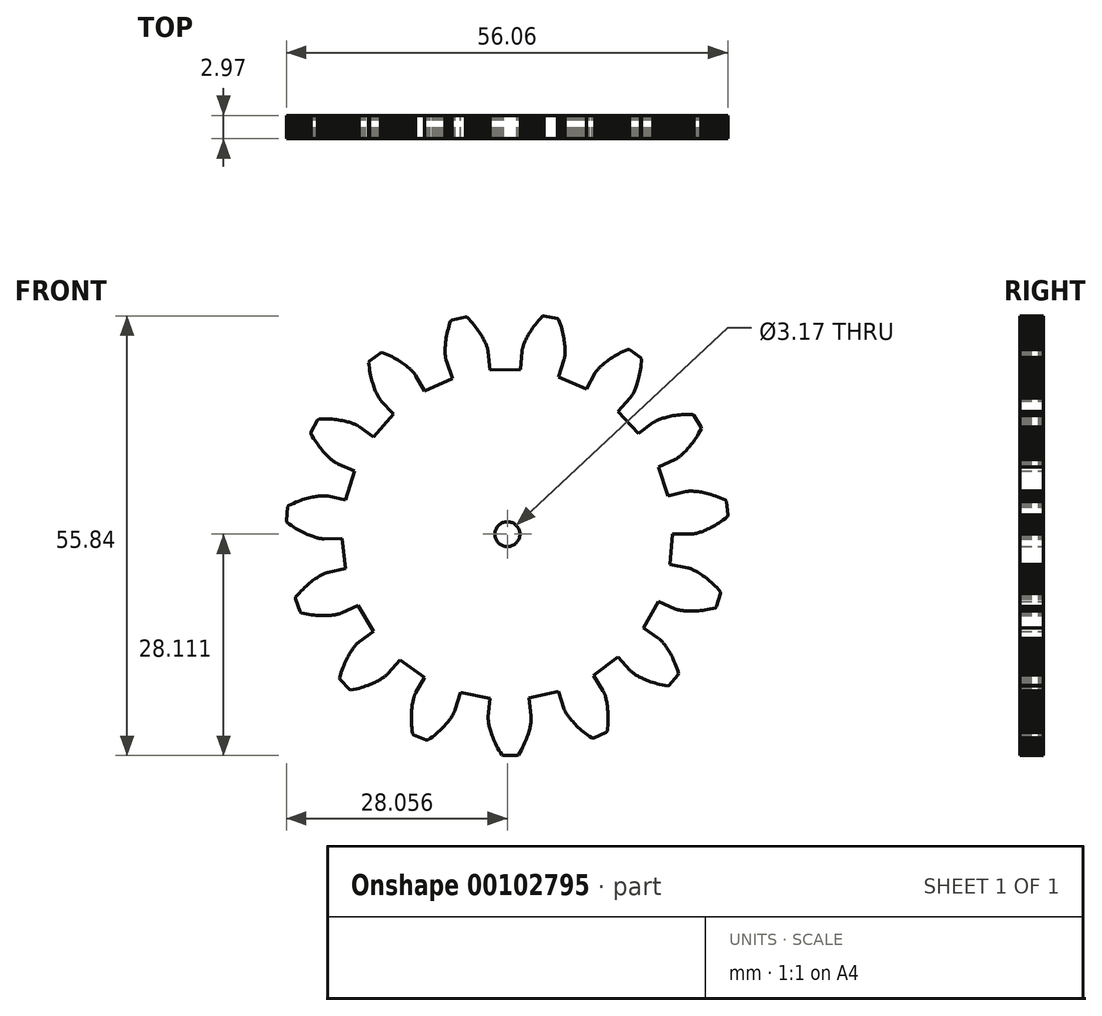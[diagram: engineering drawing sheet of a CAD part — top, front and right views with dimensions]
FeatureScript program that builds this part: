
annotation { "Feature Type Name" : "Feature", "Feature Type Description" : "" }
export const myFeature = defineFeature(function(context is Context, id is Id, definition is map)
    precondition{}
    {
        {
            var Q0;
            Q0=qCreatedBy(makeId("Front.planeOp"),FACE);
            var sketch = newSketch(context, id + "F0", { "sketchPlane" : qUnion([Q0])});
            skLineSegment(sketch, "E0", {"start": v(21.03, 0.2) * mm, "end": v(23.35, 0.2) * mm});
            skLineSegment(sketch, "E1", {"start": v(23.35, 0.2) * mm, "end": v(23.38, 0.2) * mm});
            skLineSegment(sketch, "E2", {"start": v(23.38, 0.2) * mm, "end": v(23.42, 0.2) * mm});
            skLineSegment(sketch, "E3", {"start": v(23.42, 0.2) * mm, "end": v(23.48, 0.2) * mm});
            skLineSegment(sketch, "E4", {"start": v(23.48, 0.2) * mm, "end": v(23.54, 0.2) * mm});
            skLineSegment(sketch, "E5", {"start": v(23.54, 0.2) * mm, "end": v(23.62, 0.22) * mm});
            skLineSegment(sketch, "E6", {"start": v(23.62, 0.22) * mm, "end": v(23.71, 0.24) * mm});
            skLineSegment(sketch, "E7", {"start": v(23.71, 0.24) * mm, "end": v(23.81, 0.26) * mm});
            skLineSegment(sketch, "E8", {"start": v(23.81, 0.26) * mm, "end": v(23.93, 0.28) * mm});
            skLineSegment(sketch, "E9", {"start": v(23.93, 0.28) * mm, "end": v(24.05, 0.31) * mm});
            skLineSegment(sketch, "E10", {"start": v(24.05, 0.31) * mm, "end": v(24.2, 0.35) * mm});
            skLineSegment(sketch, "E11", {"start": v(24.2, 0.35) * mm, "end": v(24.34, 0.4) * mm});
            skLineSegment(sketch, "E12", {"start": v(24.34, 0.4) * mm, "end": v(24.5, 0.44) * mm});
            skLineSegment(sketch, "E13", {"start": v(24.5, 0.44) * mm, "end": v(24.67, 0.5) * mm});
            skLineSegment(sketch, "E14", {"start": v(24.67, 0.5) * mm, "end": v(24.85, 0.57) * mm});
            skLineSegment(sketch, "E15", {"start": v(24.85, 0.57) * mm, "end": v(25.04, 0.64) * mm});
            skLineSegment(sketch, "E16", {"start": v(25.04, 0.64) * mm, "end": v(25.24, 0.73) * mm});
            skLineSegment(sketch, "E17", {"start": v(25.24, 0.73) * mm, "end": v(25.45, 0.83) * mm});
            skLineSegment(sketch, "E18", {"start": v(25.45, 0.83) * mm, "end": v(25.67, 0.93) * mm});
            skLineSegment(sketch, "E19", {"start": v(25.67, 0.93) * mm, "end": v(25.9, 1.05) * mm});
            skLineSegment(sketch, "E20", {"start": v(25.9, 1.05) * mm, "end": v(26.13, 1.17) * mm});
            skLineSegment(sketch, "E21", {"start": v(26.13, 1.17) * mm, "end": v(26.38, 1.31) * mm});
            skLineSegment(sketch, "E22", {"start": v(26.38, 1.31) * mm, "end": v(26.63, 1.46) * mm});
            skLineSegment(sketch, "E23", {"start": v(26.63, 1.46) * mm, "end": v(26.89, 1.63) * mm});
            skLineSegment(sketch, "E24", {"start": v(26.89, 1.63) * mm, "end": v(27.15, 1.8) * mm});
            skLineSegment(sketch, "E25", {"start": v(27.15, 1.8) * mm, "end": v(27.42, 2) * mm});
            skLineSegment(sketch, "E26", {"start": v(27.42, 2) * mm, "end": v(27.7, 2.2) * mm});
            skLineSegment(sketch, "E27", {"start": v(27.7, 2.2) * mm, "end": v(27.98, 2.42) * mm});
            skLineSegment(sketch, "E28", {"start": v(27.98, 2.42) * mm, "end": v(28.03, 2.63) * mm});
            skLineSegment(sketch, "E29", {"start": v(28.03, 2.63) * mm, "end": v(27.83, 4.33) * mm});
            skLineSegment(sketch, "E30", {"start": v(27.83, 4.33) * mm, "end": v(27.73, 4.53) * mm});
            skLineSegment(sketch, "E31", {"start": v(27.73, 4.53) * mm, "end": v(27.4, 4.67) * mm});
            skLineSegment(sketch, "E32", {"start": v(27.4, 4.67) * mm, "end": v(27.1, 4.8) * mm});
            skLineSegment(sketch, "E33", {"start": v(27.1, 4.8) * mm, "end": v(26.78, 4.93) * mm});
            skLineSegment(sketch, "E34", {"start": v(26.78, 4.93) * mm, "end": v(26.48, 5.04) * mm});
            skLineSegment(sketch, "E35", {"start": v(26.48, 5.04) * mm, "end": v(26.2, 5.14) * mm});
            skLineSegment(sketch, "E36", {"start": v(26.2, 5.14) * mm, "end": v(25.91, 5.23) * mm});
            skLineSegment(sketch, "E37", {"start": v(25.91, 5.23) * mm, "end": v(25.65, 5.3) * mm});
            skLineSegment(sketch, "E38", {"start": v(25.65, 5.3) * mm, "end": v(25.39, 5.37) * mm});
            skLineSegment(sketch, "E39", {"start": v(25.39, 5.37) * mm, "end": v(25.14, 5.44) * mm});
            skLineSegment(sketch, "E40", {"start": v(25.14, 5.44) * mm, "end": v(24.9, 5.49) * mm});
            skLineSegment(sketch, "E41", {"start": v(24.9, 5.49) * mm, "end": v(24.67, 5.53) * mm});
            skLineSegment(sketch, "E42", {"start": v(24.67, 5.53) * mm, "end": v(24.46, 5.57) * mm});
            skLineSegment(sketch, "E43", {"start": v(24.46, 5.57) * mm, "end": v(24.26, 5.6) * mm});
            skLineSegment(sketch, "E44", {"start": v(24.26, 5.6) * mm, "end": v(24.06, 5.62) * mm});
            skLineSegment(sketch, "E45", {"start": v(24.06, 5.62) * mm, "end": v(23.89, 5.64) * mm});
            skLineSegment(sketch, "E46", {"start": v(23.89, 5.64) * mm, "end": v(23.72, 5.65) * mm});
            skLineSegment(sketch, "E47", {"start": v(23.72, 5.65) * mm, "end": v(23.56, 5.66) * mm});
            skLineSegment(sketch, "E48", {"start": v(23.56, 5.66) * mm, "end": v(23.42, 5.66) * mm});
            skLineSegment(sketch, "E49", {"start": v(23.42, 5.66) * mm, "end": v(23.3, 5.66) * mm});
            skLineSegment(sketch, "E50", {"start": v(23.3, 5.66) * mm, "end": v(23.18, 5.66) * mm});
            skLineSegment(sketch, "E51", {"start": v(23.18, 5.66) * mm, "end": v(23.07, 5.65) * mm});
            skLineSegment(sketch, "E52", {"start": v(23.07, 5.65) * mm, "end": v(22.98, 5.65) * mm});
            skLineSegment(sketch, "E53", {"start": v(22.98, 5.65) * mm, "end": v(22.9, 5.64) * mm});
            skLineSegment(sketch, "E54", {"start": v(22.9, 5.64) * mm, "end": v(22.84, 5.63) * mm});
            skLineSegment(sketch, "E55", {"start": v(22.84, 5.63) * mm, "end": v(22.78, 5.63) * mm});
            skLineSegment(sketch, "E56", {"start": v(22.78, 5.63) * mm, "end": v(22.74, 5.62) * mm});
            skLineSegment(sketch, "E57", {"start": v(22.74, 5.62) * mm, "end": v(22.72, 5.61) * mm});
            skLineSegment(sketch, "E58", {"start": v(22.72, 5.61) * mm, "end": v(22.7, 5.61) * mm});
            skLineSegment(sketch, "E59", {"start": v(22.7, 5.61) * mm, "end": v(20.45, 5.07) * mm});
            skLineSegment(sketch, "E60", {"start": v(20.45, 5.07) * mm, "end": v(19.21, 8.73) * mm});
            skLineSegment(sketch, "E61", {"start": v(19.21, 8.73) * mm, "end": v(21.32, 9.67) * mm});
            skLineSegment(sketch, "E62", {"start": v(21.32, 9.67) * mm, "end": v(21.34, 9.68) * mm});
            skLineSegment(sketch, "E63", {"start": v(21.34, 9.68) * mm, "end": v(21.36, 9.7) * mm});
            skLineSegment(sketch, "E64", {"start": v(21.36, 9.7) * mm, "end": v(21.4, 9.71) * mm});
            skLineSegment(sketch, "E65", {"start": v(21.4, 9.71) * mm, "end": v(21.45, 9.74) * mm});
            skLineSegment(sketch, "E66", {"start": v(21.45, 9.74) * mm, "end": v(21.5, 9.77) * mm});
            skLineSegment(sketch, "E67", {"start": v(21.5, 9.77) * mm, "end": v(21.57, 9.82) * mm});
            skLineSegment(sketch, "E68", {"start": v(21.57, 9.82) * mm, "end": v(21.64, 9.87) * mm});
            skLineSegment(sketch, "E69", {"start": v(21.64, 9.87) * mm, "end": v(21.73, 9.93) * mm});
            skLineSegment(sketch, "E70", {"start": v(21.73, 9.93) * mm, "end": v(21.82, 10) * mm});
            skLineSegment(sketch, "E71", {"start": v(21.82, 10) * mm, "end": v(21.93, 10.07) * mm});
            skLineSegment(sketch, "E72", {"start": v(21.93, 10.07) * mm, "end": v(22.04, 10.16) * mm});
            skLineSegment(sketch, "E73", {"start": v(22.04, 10.16) * mm, "end": v(22.15, 10.26) * mm});
            skLineSegment(sketch, "E74", {"start": v(22.15, 10.26) * mm, "end": v(22.28, 10.38) * mm});
            skLineSegment(sketch, "E75", {"start": v(22.28, 10.38) * mm, "end": v(22.41, 10.5) * mm});
            skLineSegment(sketch, "E76", {"start": v(22.41, 10.5) * mm, "end": v(22.55, 10.63) * mm});
            skLineSegment(sketch, "E77", {"start": v(22.55, 10.63) * mm, "end": v(22.7, 10.78) * mm});
            skLineSegment(sketch, "E78", {"start": v(22.7, 10.78) * mm, "end": v(22.84, 10.94) * mm});
            skLineSegment(sketch, "E79", {"start": v(22.84, 10.94) * mm, "end": v(23, 11.11) * mm});
            skLineSegment(sketch, "E80", {"start": v(23, 11.11) * mm, "end": v(23.15, 11.3) * mm});
            skLineSegment(sketch, "E81", {"start": v(23.15, 11.3) * mm, "end": v(23.31, 11.5) * mm});
            skLineSegment(sketch, "E82", {"start": v(23.31, 11.5) * mm, "end": v(23.48, 11.7) * mm});
            skLineSegment(sketch, "E83", {"start": v(23.48, 11.7) * mm, "end": v(23.64, 11.93) * mm});
            skLineSegment(sketch, "E84", {"start": v(23.64, 11.93) * mm, "end": v(23.81, 12.17) * mm});
            skLineSegment(sketch, "E85", {"start": v(23.81, 12.17) * mm, "end": v(23.98, 12.43) * mm});
            skLineSegment(sketch, "E86", {"start": v(23.98, 12.43) * mm, "end": v(24.15, 12.7) * mm});
            skLineSegment(sketch, "E87", {"start": v(24.15, 12.7) * mm, "end": v(24.32, 12.98) * mm});
            skLineSegment(sketch, "E88", {"start": v(24.32, 12.98) * mm, "end": v(24.5, 13.28) * mm});
            skLineSegment(sketch, "E89", {"start": v(24.5, 13.28) * mm, "end": v(24.66, 13.6) * mm});
            skLineSegment(sketch, "E90", {"start": v(24.66, 13.6) * mm, "end": v(24.62, 13.8) * mm});
            skLineSegment(sketch, "E91", {"start": v(24.62, 13.8) * mm, "end": v(23.74, 15.29) * mm});
            skLineSegment(sketch, "E92", {"start": v(23.74, 15.29) * mm, "end": v(23.57, 15.42) * mm});
            skLineSegment(sketch, "E93", {"start": v(23.57, 15.42) * mm, "end": v(23.22, 15.42) * mm});
            skLineSegment(sketch, "E94", {"start": v(23.22, 15.42) * mm, "end": v(22.87, 15.42) * mm});
            skLineSegment(sketch, "E95", {"start": v(22.87, 15.42) * mm, "end": v(22.54, 15.4) * mm});
            skLineSegment(sketch, "E96", {"start": v(22.54, 15.4) * mm, "end": v(22.23, 15.38) * mm});
            skLineSegment(sketch, "E97", {"start": v(22.23, 15.38) * mm, "end": v(21.92, 15.36) * mm});
            skLineSegment(sketch, "E98", {"start": v(21.92, 15.36) * mm, "end": v(21.63, 15.32) * mm});
            skLineSegment(sketch, "E99", {"start": v(21.63, 15.32) * mm, "end": v(21.35, 15.28) * mm});
            skLineSegment(sketch, "E100", {"start": v(21.35, 15.28) * mm, "end": v(21.09, 15.24) * mm});
            skLineSegment(sketch, "E101", {"start": v(21.09, 15.24) * mm, "end": v(20.83, 15.2) * mm});
            skLineSegment(sketch, "E102", {"start": v(20.83, 15.2) * mm, "end": v(20.6, 15.15) * mm});
            skLineSegment(sketch, "E103", {"start": v(20.6, 15.15) * mm, "end": v(20.37, 15.1) * mm});
            skLineSegment(sketch, "E104", {"start": v(20.37, 15.1) * mm, "end": v(20.16, 15.04) * mm});
            skLineSegment(sketch, "E105", {"start": v(20.16, 15.04) * mm, "end": v(19.96, 14.98) * mm});
            skLineSegment(sketch, "E106", {"start": v(19.96, 14.98) * mm, "end": v(19.78, 14.93) * mm});
            skLineSegment(sketch, "E107", {"start": v(19.78, 14.93) * mm, "end": v(19.6, 14.87) * mm});
            skLineSegment(sketch, "E108", {"start": v(19.6, 14.87) * mm, "end": v(19.45, 14.81) * mm});
            skLineSegment(sketch, "E109", {"start": v(19.45, 14.81) * mm, "end": v(19.3, 14.76) * mm});
            skLineSegment(sketch, "E110", {"start": v(19.3, 14.76) * mm, "end": v(19.18, 14.7) * mm});
            skLineSegment(sketch, "E111", {"start": v(19.18, 14.7) * mm, "end": v(19.06, 14.65) * mm});
            skLineSegment(sketch, "E112", {"start": v(19.06, 14.65) * mm, "end": v(18.95, 14.6) * mm});
            skLineSegment(sketch, "E113", {"start": v(18.95, 14.6) * mm, "end": v(18.86, 14.55) * mm});
            skLineSegment(sketch, "E114", {"start": v(18.86, 14.55) * mm, "end": v(18.78, 14.51) * mm});
            skLineSegment(sketch, "E115", {"start": v(18.78, 14.51) * mm, "end": v(18.7, 14.47) * mm});
            skLineSegment(sketch, "E116", {"start": v(18.7, 14.47) * mm, "end": v(18.65, 14.44) * mm});
            skLineSegment(sketch, "E117", {"start": v(18.65, 14.44) * mm, "end": v(18.6, 14.41) * mm});
            skLineSegment(sketch, "E118", {"start": v(18.6, 14.41) * mm, "end": v(18.57, 14.4) * mm});
            skLineSegment(sketch, "E119", {"start": v(18.57, 14.4) * mm, "end": v(18.55, 14.37) * mm});
            skLineSegment(sketch, "E120", {"start": v(18.55, 14.37) * mm, "end": v(18.53, 14.36) * mm});
            skLineSegment(sketch, "E121", {"start": v(18.53, 14.36) * mm, "end": v(16.7, 12.96) * mm});
            skLineSegment(sketch, "E122", {"start": v(16.7, 12.96) * mm, "end": v(14.08, 15.8) * mm});
            skLineSegment(sketch, "E123", {"start": v(14.08, 15.8) * mm, "end": v(15.63, 17.52) * mm});
            skLineSegment(sketch, "E124", {"start": v(15.63, 17.52) * mm, "end": v(15.64, 17.53) * mm});
            skLineSegment(sketch, "E125", {"start": v(15.64, 17.53) * mm, "end": v(15.65, 17.55) * mm});
            skLineSegment(sketch, "E126", {"start": v(15.65, 17.55) * mm, "end": v(15.68, 17.58) * mm});
            skLineSegment(sketch, "E127", {"start": v(15.68, 17.58) * mm, "end": v(15.7, 17.63) * mm});
            skLineSegment(sketch, "E128", {"start": v(15.7, 17.63) * mm, "end": v(15.75, 17.68) * mm});
            skLineSegment(sketch, "E129", {"start": v(15.75, 17.68) * mm, "end": v(15.8, 17.75) * mm});
            skLineSegment(sketch, "E130", {"start": v(15.8, 17.75) * mm, "end": v(15.84, 17.82) * mm});
            skLineSegment(sketch, "E131", {"start": v(15.84, 17.82) * mm, "end": v(15.9, 17.91) * mm});
            skLineSegment(sketch, "E132", {"start": v(15.9, 17.91) * mm, "end": v(15.95, 18.01) * mm});
            skLineSegment(sketch, "E133", {"start": v(15.95, 18.01) * mm, "end": v(16.01, 18.13) * mm});
            skLineSegment(sketch, "E134", {"start": v(16.01, 18.13) * mm, "end": v(16.08, 18.25) * mm});
            skLineSegment(sketch, "E135", {"start": v(16.08, 18.25) * mm, "end": v(16.14, 18.4) * mm});
            skLineSegment(sketch, "E136", {"start": v(16.14, 18.4) * mm, "end": v(16.21, 18.55) * mm});
            skLineSegment(sketch, "E137", {"start": v(16.21, 18.55) * mm, "end": v(16.28, 18.71) * mm});
            skLineSegment(sketch, "E138", {"start": v(16.28, 18.71) * mm, "end": v(16.35, 18.9) * mm});
            skLineSegment(sketch, "E139", {"start": v(16.35, 18.9) * mm, "end": v(16.43, 19.08) * mm});
            skLineSegment(sketch, "E140", {"start": v(16.43, 19.08) * mm, "end": v(16.5, 19.29) * mm});
            skLineSegment(sketch, "E141", {"start": v(16.5, 19.29) * mm, "end": v(16.57, 19.5) * mm});
            skLineSegment(sketch, "E142", {"start": v(16.57, 19.5) * mm, "end": v(16.64, 19.74) * mm});
            skLineSegment(sketch, "E143", {"start": v(16.64, 19.74) * mm, "end": v(16.7, 19.99) * mm});
            skLineSegment(sketch, "E144", {"start": v(16.7, 19.99) * mm, "end": v(16.77, 20.25) * mm});
            skLineSegment(sketch, "E145", {"start": v(16.77, 20.25) * mm, "end": v(16.82, 20.52) * mm});
            skLineSegment(sketch, "E146", {"start": v(16.82, 20.52) * mm, "end": v(16.88, 20.81) * mm});
            skLineSegment(sketch, "E147", {"start": v(16.88, 20.81) * mm, "end": v(16.93, 21.11) * mm});
            skLineSegment(sketch, "E148", {"start": v(16.93, 21.11) * mm, "end": v(16.98, 21.43) * mm});
            skLineSegment(sketch, "E149", {"start": v(16.98, 21.43) * mm, "end": v(17.02, 21.76) * mm});
            skLineSegment(sketch, "E150", {"start": v(17.02, 21.76) * mm, "end": v(17.05, 22.1) * mm});
            skLineSegment(sketch, "E151", {"start": v(17.05, 22.1) * mm, "end": v(17.08, 22.46) * mm});
            skLineSegment(sketch, "E152", {"start": v(17.08, 22.46) * mm, "end": v(16.96, 22.63) * mm});
            skLineSegment(sketch, "E153", {"start": v(16.96, 22.63) * mm, "end": v(15.55, 23.63) * mm});
            skLineSegment(sketch, "E154", {"start": v(15.55, 23.63) * mm, "end": v(15.34, 23.68) * mm});
            skLineSegment(sketch, "E155", {"start": v(15.34, 23.68) * mm, "end": v(15.02, 23.54) * mm});
            skLineSegment(sketch, "E156", {"start": v(15.02, 23.54) * mm, "end": v(14.7, 23.4) * mm});
            skLineSegment(sketch, "E157", {"start": v(14.7, 23.4) * mm, "end": v(14.4, 23.25) * mm});
            skLineSegment(sketch, "E158", {"start": v(14.4, 23.25) * mm, "end": v(14.13, 23.1) * mm});
            skLineSegment(sketch, "E159", {"start": v(14.13, 23.1) * mm, "end": v(13.86, 22.95) * mm});
            skLineSegment(sketch, "E160", {"start": v(13.86, 22.95) * mm, "end": v(13.6, 22.8) * mm});
            skLineSegment(sketch, "E161", {"start": v(13.6, 22.8) * mm, "end": v(13.37, 22.65) * mm});
            skLineSegment(sketch, "E162", {"start": v(13.37, 22.65) * mm, "end": v(13.14, 22.5) * mm});
            skLineSegment(sketch, "E163", {"start": v(13.14, 22.5) * mm, "end": v(12.93, 22.36) * mm});
            skLineSegment(sketch, "E164", {"start": v(12.93, 22.36) * mm, "end": v(12.73, 22.22) * mm});
            skLineSegment(sketch, "E165", {"start": v(12.73, 22.22) * mm, "end": v(12.55, 22.08) * mm});
            skLineSegment(sketch, "E166", {"start": v(12.55, 22.08) * mm, "end": v(12.38, 21.95) * mm});
            skLineSegment(sketch, "E167", {"start": v(12.38, 21.95) * mm, "end": v(12.22, 21.81) * mm});
            skLineSegment(sketch, "E168", {"start": v(12.22, 21.81) * mm, "end": v(12.08, 21.69) * mm});
            skLineSegment(sketch, "E169", {"start": v(12.08, 21.69) * mm, "end": v(11.94, 21.57) * mm});
            skLineSegment(sketch, "E170", {"start": v(11.94, 21.57) * mm, "end": v(11.82, 21.45) * mm});
            skLineSegment(sketch, "E171", {"start": v(11.82, 21.45) * mm, "end": v(11.72, 21.34) * mm});
            skLineSegment(sketch, "E172", {"start": v(11.72, 21.34) * mm, "end": v(11.62, 21.24) * mm});
            skLineSegment(sketch, "E173", {"start": v(11.62, 21.24) * mm, "end": v(11.53, 21.14) * mm});
            skLineSegment(sketch, "E174", {"start": v(11.53, 21.14) * mm, "end": v(11.45, 21.05) * mm});
            skLineSegment(sketch, "E175", {"start": v(11.45, 21.05) * mm, "end": v(11.39, 20.97) * mm});
            skLineSegment(sketch, "E176", {"start": v(11.39, 20.97) * mm, "end": v(11.33, 20.9) * mm});
            skLineSegment(sketch, "E177", {"start": v(11.33, 20.9) * mm, "end": v(11.28, 20.84) * mm});
            skLineSegment(sketch, "E178", {"start": v(11.28, 20.84) * mm, "end": v(11.24, 20.78) * mm});
            skLineSegment(sketch, "E179", {"start": v(11.24, 20.78) * mm, "end": v(11.2, 20.7) * mm});
            skLineSegment(sketch, "E180", {"start": v(11.2, 20.7) * mm, "end": v(11.18, 20.68) * mm});
            skLineSegment(sketch, "E181", {"start": v(11.18, 20.68) * mm, "end": v(11.17, 20.67) * mm});
            skLineSegment(sketch, "E182", {"start": v(11.17, 20.67) * mm, "end": v(10.07, 18.64) * mm});
            skLineSegment(sketch, "E183", {"start": v(10.07, 18.64) * mm, "end": v(6.52, 20.16) * mm});
            skLineSegment(sketch, "E184", {"start": v(6.52, 20.16) * mm, "end": v(7.23, 22.36) * mm});
            skLineSegment(sketch, "E185", {"start": v(7.23, 22.36) * mm, "end": v(7.23, 22.38) * mm});
            skLineSegment(sketch, "E186", {"start": v(7.23, 22.38) * mm, "end": v(7.24, 22.4) * mm});
            skLineSegment(sketch, "E187", {"start": v(7.24, 22.4) * mm, "end": v(7.25, 22.45) * mm});
            skLineSegment(sketch, "E188", {"start": v(7.25, 22.45) * mm, "end": v(7.26, 22.5) * mm});
            skLineSegment(sketch, "E189", {"start": v(7.26, 22.5) * mm, "end": v(7.28, 22.56) * mm});
            skLineSegment(sketch, "E190", {"start": v(7.28, 22.56) * mm, "end": v(7.29, 22.64) * mm});
            skLineSegment(sketch, "E191", {"start": v(7.29, 22.64) * mm, "end": v(7.3, 22.73) * mm});
            skLineSegment(sketch, "E192", {"start": v(7.3, 22.73) * mm, "end": v(7.31, 22.83) * mm});
            skLineSegment(sketch, "E193", {"start": v(7.31, 22.83) * mm, "end": v(7.33, 22.95) * mm});
            skLineSegment(sketch, "E194", {"start": v(7.33, 22.95) * mm, "end": v(7.34, 23.08) * mm});
            skLineSegment(sketch, "E195", {"start": v(7.34, 23.08) * mm, "end": v(7.34, 23.22) * mm});
            skLineSegment(sketch, "E196", {"start": v(7.34, 23.22) * mm, "end": v(7.35, 23.38) * mm});
            skLineSegment(sketch, "E197", {"start": v(7.35, 23.38) * mm, "end": v(7.35, 23.54) * mm});
            skLineSegment(sketch, "E198", {"start": v(7.35, 23.54) * mm, "end": v(7.34, 23.72) * mm});
            skLineSegment(sketch, "E199", {"start": v(7.34, 23.72) * mm, "end": v(7.34, 23.92) * mm});
            skLineSegment(sketch, "E200", {"start": v(7.34, 23.92) * mm, "end": v(7.32, 24.12) * mm});
            skLineSegment(sketch, "E201", {"start": v(7.32, 24.12) * mm, "end": v(7.3, 24.34) * mm});
            skLineSegment(sketch, "E202", {"start": v(7.3, 24.34) * mm, "end": v(7.28, 24.57) * mm});
            skLineSegment(sketch, "E203", {"start": v(7.28, 24.57) * mm, "end": v(7.25, 24.8) * mm});
            skLineSegment(sketch, "E204", {"start": v(7.25, 24.8) * mm, "end": v(7.2, 25.06) * mm});
            skLineSegment(sketch, "E205", {"start": v(7.2, 25.06) * mm, "end": v(7.16, 25.32) * mm});
            skLineSegment(sketch, "E206", {"start": v(7.16, 25.32) * mm, "end": v(7.1, 25.6) * mm});
            skLineSegment(sketch, "E207", {"start": v(7.1, 25.6) * mm, "end": v(7.04, 25.88) * mm});
            skLineSegment(sketch, "E208", {"start": v(7.04, 25.88) * mm, "end": v(6.96, 26.18) * mm});
            skLineSegment(sketch, "E209", {"start": v(6.96, 26.18) * mm, "end": v(6.87, 26.49) * mm});
            skLineSegment(sketch, "E210", {"start": v(6.87, 26.49) * mm, "end": v(6.78, 26.8) * mm});
            skLineSegment(sketch, "E211", {"start": v(6.78, 26.8) * mm, "end": v(6.67, 27.13) * mm});
            skLineSegment(sketch, "E212", {"start": v(6.67, 27.13) * mm, "end": v(6.55, 27.47) * mm});
            skLineSegment(sketch, "E213", {"start": v(6.55, 27.47) * mm, "end": v(6.36, 27.58) * mm});
            skLineSegment(sketch, "E214", {"start": v(6.36, 27.58) * mm, "end": v(4.68, 27.92) * mm});
            skLineSegment(sketch, "E215", {"start": v(4.68, 27.92) * mm, "end": v(4.46, 27.88) * mm});
            skLineSegment(sketch, "E216", {"start": v(4.46, 27.88) * mm, "end": v(4.22, 27.62) * mm});
            skLineSegment(sketch, "E217", {"start": v(4.22, 27.62) * mm, "end": v(4, 27.36) * mm});
            skLineSegment(sketch, "E218", {"start": v(4, 27.36) * mm, "end": v(3.79, 27.1) * mm});
            skLineSegment(sketch, "E219", {"start": v(3.79, 27.1) * mm, "end": v(3.6, 26.85) * mm});
            skLineSegment(sketch, "E220", {"start": v(3.6, 26.85) * mm, "end": v(3.4, 26.6) * mm});
            skLineSegment(sketch, "E221", {"start": v(3.4, 26.6) * mm, "end": v(3.24, 26.37) * mm});
            skLineSegment(sketch, "E222", {"start": v(3.24, 26.37) * mm, "end": v(3.08, 26.14) * mm});
            skLineSegment(sketch, "E223", {"start": v(3.08, 26.14) * mm, "end": v(2.93, 25.91) * mm});
            skLineSegment(sketch, "E224", {"start": v(2.93, 25.91) * mm, "end": v(2.8, 25.7) * mm});
            skLineSegment(sketch, "E225", {"start": v(2.8, 25.7) * mm, "end": v(2.68, 25.48) * mm});
            skLineSegment(sketch, "E226", {"start": v(2.68, 25.48) * mm, "end": v(2.57, 25.28) * mm});
            skLineSegment(sketch, "E227", {"start": v(2.57, 25.28) * mm, "end": v(2.47, 25.09) * mm});
            skLineSegment(sketch, "E228", {"start": v(2.47, 25.09) * mm, "end": v(2.37, 24.9) * mm});
            skLineSegment(sketch, "E229", {"start": v(2.37, 24.9) * mm, "end": v(2.3, 24.73) * mm});
            skLineSegment(sketch, "E230", {"start": v(2.3, 24.73) * mm, "end": v(2.22, 24.57) * mm});
            skLineSegment(sketch, "E231", {"start": v(2.22, 24.57) * mm, "end": v(2.16, 24.41) * mm});
            skLineSegment(sketch, "E232", {"start": v(2.16, 24.41) * mm, "end": v(2.1, 24.27) * mm});
            skLineSegment(sketch, "E233", {"start": v(2.1, 24.27) * mm, "end": v(2.05, 24.13) * mm});
            skLineSegment(sketch, "E234", {"start": v(2.05, 24.13) * mm, "end": v(2.01, 24) * mm});
            skLineSegment(sketch, "E235", {"start": v(2.01, 24) * mm, "end": v(1.98, 23.9) * mm});
            skLineSegment(sketch, "E236", {"start": v(1.98, 23.9) * mm, "end": v(1.95, 23.8) * mm});
            skLineSegment(sketch, "E237", {"start": v(1.95, 23.8) * mm, "end": v(1.93, 23.7) * mm});
            skLineSegment(sketch, "E238", {"start": v(1.93, 23.7) * mm, "end": v(1.91, 23.63) * mm});
            skLineSegment(sketch, "E239", {"start": v(1.91, 23.63) * mm, "end": v(1.9, 23.57) * mm});
            skLineSegment(sketch, "E240", {"start": v(1.9, 23.57) * mm, "end": v(1.89, 23.51) * mm});
            skLineSegment(sketch, "E241", {"start": v(1.89, 23.51) * mm, "end": v(1.88, 23.47) * mm});
            skLineSegment(sketch, "E242", {"start": v(1.88, 23.47) * mm, "end": v(1.88, 23.45) * mm});
            skLineSegment(sketch, "E243", {"start": v(1.88, 23.45) * mm, "end": v(1.88, 23.43) * mm});
            skLineSegment(sketch, "E244", {"start": v(1.88, 23.43) * mm, "end": v(1.7, 21.13) * mm});
            skLineSegment(sketch, "E245", {"start": v(1.7, 21.13) * mm, "end": v(-2.17, 21.08) * mm});
            skLineSegment(sketch, "E246", {"start": v(-2.17, 21.08) * mm, "end": v(-2.41, 23.38) * mm});
            skLineSegment(sketch, "E247", {"start": v(-2.41, 23.38) * mm, "end": v(-2.41, 23.4) * mm});
            skLineSegment(sketch, "E248", {"start": v(-2.41, 23.4) * mm, "end": v(-2.42, 23.42) * mm});
            skLineSegment(sketch, "E249", {"start": v(-2.42, 23.42) * mm, "end": v(-2.42, 23.46) * mm});
            skLineSegment(sketch, "E250", {"start": v(-2.42, 23.46) * mm, "end": v(-2.43, 23.51) * mm});
            skLineSegment(sketch, "E251", {"start": v(-2.43, 23.51) * mm, "end": v(-2.45, 23.58) * mm});
            skLineSegment(sketch, "E252", {"start": v(-2.45, 23.58) * mm, "end": v(-2.47, 23.65) * mm});
            skLineSegment(sketch, "E253", {"start": v(-2.47, 23.65) * mm, "end": v(-2.5, 23.74) * mm});
            skLineSegment(sketch, "E254", {"start": v(-2.5, 23.74) * mm, "end": v(-2.52, 23.84) * mm});
            skLineSegment(sketch, "E255", {"start": v(-2.52, 23.84) * mm, "end": v(-2.56, 23.95) * mm});
            skLineSegment(sketch, "E256", {"start": v(-2.56, 23.95) * mm, "end": v(-2.6, 24.07) * mm});
            skLineSegment(sketch, "E257", {"start": v(-2.6, 24.07) * mm, "end": v(-2.66, 24.2) * mm});
            skLineSegment(sketch, "E258", {"start": v(-2.66, 24.2) * mm, "end": v(-2.71, 24.35) * mm});
            skLineSegment(sketch, "E259", {"start": v(-2.71, 24.35) * mm, "end": v(-2.78, 24.5) * mm});
            skLineSegment(sketch, "E260", {"start": v(-2.78, 24.5) * mm, "end": v(-2.86, 24.67) * mm});
            skLineSegment(sketch, "E261", {"start": v(-2.86, 24.67) * mm, "end": v(-2.94, 24.84) * mm});
            skLineSegment(sketch, "E262", {"start": v(-2.94, 24.84) * mm, "end": v(-3.04, 25.02) * mm});
            skLineSegment(sketch, "E263", {"start": v(-3.04, 25.02) * mm, "end": v(-3.14, 25.2) * mm});
            skLineSegment(sketch, "E264", {"start": v(-3.14, 25.2) * mm, "end": v(-3.26, 25.4) * mm});
            skLineSegment(sketch, "E265", {"start": v(-3.26, 25.4) * mm, "end": v(-3.39, 25.62) * mm});
            skLineSegment(sketch, "E266", {"start": v(-3.39, 25.62) * mm, "end": v(-3.53, 25.83) * mm});
            skLineSegment(sketch, "E267", {"start": v(-3.53, 25.83) * mm, "end": v(-3.68, 26.05) * mm});
            skLineSegment(sketch, "E268", {"start": v(-3.68, 26.05) * mm, "end": v(-3.84, 26.28) * mm});
            skLineSegment(sketch, "E269", {"start": v(-3.84, 26.28) * mm, "end": v(-4.02, 26.51) * mm});
            skLineSegment(sketch, "E270", {"start": v(-4.02, 26.51) * mm, "end": v(-4.2, 26.75) * mm});
            skLineSegment(sketch, "E271", {"start": v(-4.2, 26.75) * mm, "end": v(-4.41, 27) * mm});
            skLineSegment(sketch, "E272", {"start": v(-4.41, 27) * mm, "end": v(-4.63, 27.25) * mm});
            skLineSegment(sketch, "E273", {"start": v(-4.63, 27.25) * mm, "end": v(-4.86, 27.5) * mm});
            skLineSegment(sketch, "E274", {"start": v(-4.86, 27.5) * mm, "end": v(-5.1, 27.76) * mm});
            skLineSegment(sketch, "E275", {"start": v(-5.1, 27.76) * mm, "end": v(-5.32, 27.79) * mm});
            skLineSegment(sketch, "E276", {"start": v(-5.32, 27.79) * mm, "end": v(-7, 27.41) * mm});
            skLineSegment(sketch, "E277", {"start": v(-7, 27.41) * mm, "end": v(-7.18, 27.3) * mm});
            skLineSegment(sketch, "E278", {"start": v(-7.18, 27.3) * mm, "end": v(-7.3, 26.95) * mm});
            skLineSegment(sketch, "E279", {"start": v(-7.3, 26.95) * mm, "end": v(-7.4, 26.63) * mm});
            skLineSegment(sketch, "E280", {"start": v(-7.4, 26.63) * mm, "end": v(-7.48, 26.3) * mm});
            skLineSegment(sketch, "E281", {"start": v(-7.48, 26.3) * mm, "end": v(-7.56, 26) * mm});
            skLineSegment(sketch, "E282", {"start": v(-7.56, 26) * mm, "end": v(-7.63, 25.7) * mm});
            skLineSegment(sketch, "E283", {"start": v(-7.63, 25.7) * mm, "end": v(-7.69, 25.41) * mm});
            skLineSegment(sketch, "E284", {"start": v(-7.69, 25.41) * mm, "end": v(-7.74, 25.14) * mm});
            skLineSegment(sketch, "E285", {"start": v(-7.74, 25.14) * mm, "end": v(-7.78, 24.87) * mm});
            skLineSegment(sketch, "E286", {"start": v(-7.78, 24.87) * mm, "end": v(-7.81, 24.62) * mm});
            skLineSegment(sketch, "E287", {"start": v(-7.81, 24.62) * mm, "end": v(-7.84, 24.38) * mm});
            skLineSegment(sketch, "E288", {"start": v(-7.84, 24.38) * mm, "end": v(-7.86, 24.15) * mm});
            skLineSegment(sketch, "E289", {"start": v(-7.86, 24.15) * mm, "end": v(-7.87, 23.93) * mm});
            skLineSegment(sketch, "E290", {"start": v(-7.87, 23.93) * mm, "end": v(-7.88, 23.72) * mm});
            skLineSegment(sketch, "E291", {"start": v(-7.88, 23.72) * mm, "end": v(-7.88, 23.53) * mm});
            skLineSegment(sketch, "E292", {"start": v(-7.88, 23.53) * mm, "end": v(-7.88, 23.35) * mm});
            skLineSegment(sketch, "E293", {"start": v(-7.88, 23.35) * mm, "end": v(-7.88, 23.18) * mm});
            skLineSegment(sketch, "E294", {"start": v(-7.88, 23.18) * mm, "end": v(-7.87, 23.03) * mm});
            skLineSegment(sketch, "E295", {"start": v(-7.87, 23.03) * mm, "end": v(-7.86, 22.89) * mm});
            skLineSegment(sketch, "E296", {"start": v(-7.86, 22.89) * mm, "end": v(-7.85, 22.76) * mm});
            skLineSegment(sketch, "E297", {"start": v(-7.85, 22.76) * mm, "end": v(-7.83, 22.64) * mm});
            skLineSegment(sketch, "E298", {"start": v(-7.83, 22.64) * mm, "end": v(-7.81, 22.54) * mm});
            skLineSegment(sketch, "E299", {"start": v(-7.81, 22.54) * mm, "end": v(-7.8, 22.45) * mm});
            skLineSegment(sketch, "E300", {"start": v(-7.8, 22.45) * mm, "end": v(-7.78, 22.37) * mm});
            skLineSegment(sketch, "E301", {"start": v(-7.78, 22.37) * mm, "end": v(-7.77, 22.3) * mm});
            skLineSegment(sketch, "E302", {"start": v(-7.77, 22.3) * mm, "end": v(-7.76, 22.26) * mm});
            skLineSegment(sketch, "E303", {"start": v(-7.76, 22.26) * mm, "end": v(-7.75, 22.22) * mm});
            skLineSegment(sketch, "E304", {"start": v(-7.75, 22.22) * mm, "end": v(-7.74, 22.19) * mm});
            skLineSegment(sketch, "E305", {"start": v(-7.74, 22.19) * mm, "end": v(-7.73, 22.17) * mm});
            skLineSegment(sketch, "E306", {"start": v(-7.73, 22.17) * mm, "end": v(-6.96, 20) * mm});
            skLineSegment(sketch, "E307", {"start": v(-6.96, 20) * mm, "end": v(-10.47, 18.38) * mm});
            skLineSegment(sketch, "E308", {"start": v(-10.47, 18.38) * mm, "end": v(-11.63, 20.38) * mm});
            skLineSegment(sketch, "E309", {"start": v(-11.63, 20.38) * mm, "end": v(-11.64, 20.4) * mm});
            skLineSegment(sketch, "E310", {"start": v(-11.64, 20.4) * mm, "end": v(-11.65, 20.42) * mm});
            skLineSegment(sketch, "E311", {"start": v(-11.65, 20.42) * mm, "end": v(-11.68, 20.45) * mm});
            skLineSegment(sketch, "E312", {"start": v(-11.68, 20.45) * mm, "end": v(-11.7, 20.5) * mm});
            skLineSegment(sketch, "E313", {"start": v(-11.7, 20.5) * mm, "end": v(-11.75, 20.55) * mm});
            skLineSegment(sketch, "E314", {"start": v(-11.8, 20.6) * mm, "end": v(-11.86, 20.68) * mm});
            skLineSegment(sketch, "E315", {"start": v(-11.86, 20.68) * mm, "end": v(-11.92, 20.76) * mm});
            skLineSegment(sketch, "E316", {"start": v(-11.92, 20.76) * mm, "end": v(-12, 20.85) * mm});
            skLineSegment(sketch, "E317", {"start": v(-12, 20.85) * mm, "end": v(-12.1, 20.94) * mm});
            skLineSegment(sketch, "E318", {"start": v(-12.1, 20.94) * mm, "end": v(-12.2, 21.04) * mm});
            skLineSegment(sketch, "E319", {"start": v(-12.2, 21.04) * mm, "end": v(-12.3, 21.15) * mm});
            skLineSegment(sketch, "E320", {"start": v(-12.3, 21.15) * mm, "end": v(-12.43, 21.26) * mm});
            skLineSegment(sketch, "E321", {"start": v(-12.43, 21.26) * mm, "end": v(-12.56, 21.38) * mm});
            skLineSegment(sketch, "E322", {"start": v(-12.56, 21.38) * mm, "end": v(-12.71, 21.5) * mm});
            skLineSegment(sketch, "E323", {"start": v(-12.71, 21.5) * mm, "end": v(-12.87, 21.63) * mm});
            skLineSegment(sketch, "E324", {"start": v(-12.87, 21.63) * mm, "end": v(-13.05, 21.76) * mm});
            skLineSegment(sketch, "E325", {"start": v(-13.05, 21.76) * mm, "end": v(-13.23, 21.9) * mm});
            skLineSegment(sketch, "E326", {"start": v(-13.23, 21.9) * mm, "end": v(-13.43, 22.03) * mm});
            skLineSegment(sketch, "E327", {"start": v(-13.43, 22.03) * mm, "end": v(-13.65, 22.17) * mm});
            skLineSegment(sketch, "E328", {"start": v(-13.65, 22.17) * mm, "end": v(-13.88, 22.3) * mm});
            skLineSegment(sketch, "E329", {"start": v(-13.88, 22.3) * mm, "end": v(-14.12, 22.45) * mm});
            skLineSegment(sketch, "E330", {"start": v(-14.12, 22.45) * mm, "end": v(-14.38, 22.6) * mm});
            skLineSegment(sketch, "E331", {"start": v(-14.38, 22.6) * mm, "end": v(-14.65, 22.73) * mm});
            skLineSegment(sketch, "E332", {"start": v(-14.65, 22.73) * mm, "end": v(-14.93, 22.88) * mm});
            skLineSegment(sketch, "E333", {"start": v(-14.93, 22.88) * mm, "end": v(-15.23, 23.02) * mm});
            skLineSegment(sketch, "E334", {"start": v(-15.23, 23.02) * mm, "end": v(-15.55, 23.16) * mm});
            skLineSegment(sketch, "E335", {"start": v(-15.55, 23.16) * mm, "end": v(-15.88, 23.3) * mm});
            skLineSegment(sketch, "E336", {"start": v(-15.88, 23.3) * mm, "end": v(-16.09, 23.23) * mm});
            skLineSegment(sketch, "E337", {"start": v(-16.09, 23.23) * mm, "end": v(-17.46, 22.2) * mm});
            skLineSegment(sketch, "E338", {"start": v(-17.46, 22.2) * mm, "end": v(-17.58, 22.02) * mm});
            skLineSegment(sketch, "E339", {"start": v(-17.58, 22.02) * mm, "end": v(-17.55, 21.66) * mm});
            skLineSegment(sketch, "E340", {"start": v(-17.55, 21.66) * mm, "end": v(-17.5, 21.32) * mm});
            skLineSegment(sketch, "E341", {"start": v(-17.5, 21.32) * mm, "end": v(-17.46, 21) * mm});
            skLineSegment(sketch, "E342", {"start": v(-17.46, 21) * mm, "end": v(-17.4, 20.68) * mm});
            skLineSegment(sketch, "E343", {"start": v(-17.4, 20.68) * mm, "end": v(-17.34, 20.38) * mm});
            skLineSegment(sketch, "E344", {"start": v(-17.34, 20.38) * mm, "end": v(-17.28, 20.1) * mm});
            skLineSegment(sketch, "E345", {"start": v(-17.28, 20.1) * mm, "end": v(-17.21, 19.82) * mm});
            skLineSegment(sketch, "E346", {"start": v(-17.21, 19.82) * mm, "end": v(-17.14, 19.56) * mm});
            skLineSegment(sketch, "E347", {"start": v(-17.14, 19.56) * mm, "end": v(-17.07, 19.32) * mm});
            skLineSegment(sketch, "E348", {"start": v(-17.07, 19.32) * mm, "end": v(-17, 19.09) * mm});
            skLineSegment(sketch, "E349", {"start": v(-17, 19.09) * mm, "end": v(-16.92, 18.87) * mm});
            skLineSegment(sketch, "E350", {"start": v(-16.92, 18.87) * mm, "end": v(-16.85, 18.66) * mm});
            skLineSegment(sketch, "E351", {"start": v(-16.85, 18.66) * mm, "end": v(-16.77, 18.47) * mm});
            skLineSegment(sketch, "E352", {"start": v(-16.77, 18.47) * mm, "end": v(-16.7, 18.3) * mm});
            skLineSegment(sketch, "E353", {"start": v(-16.7, 18.3) * mm, "end": v(-16.62, 18.13) * mm});
            skLineSegment(sketch, "E354", {"start": v(-16.62, 18.13) * mm, "end": v(-16.55, 17.98) * mm});
            skLineSegment(sketch, "E355", {"start": v(-16.55, 17.98) * mm, "end": v(-16.48, 17.84) * mm});
            skLineSegment(sketch, "E356", {"start": v(-16.48, 17.84) * mm, "end": v(-16.4, 17.72) * mm});
            skLineSegment(sketch, "E357", {"start": v(-16.4, 17.72) * mm, "end": v(-16.34, 17.6) * mm});
            skLineSegment(sketch, "E358", {"start": v(-16.34, 17.6) * mm, "end": v(-16.28, 17.5) * mm});
            skLineSegment(sketch, "E359", {"start": v(-16.28, 17.5) * mm, "end": v(-16.23, 17.42) * mm});
            skLineSegment(sketch, "E360", {"start": v(-16.23, 17.42) * mm, "end": v(-16.18, 17.34) * mm});
            skLineSegment(sketch, "E361", {"start": v(-16.18, 17.34) * mm, "end": v(-16.13, 17.28) * mm});
            skLineSegment(sketch, "E362", {"start": v(-16.13, 17.28) * mm, "end": v(-16.1, 17.23) * mm});
            skLineSegment(sketch, "E363", {"start": v(-16.1, 17.23) * mm, "end": v(-16.06, 17.18) * mm});
            skLineSegment(sketch, "E364", {"start": v(-16.06, 17.18) * mm, "end": v(-16.03, 17.15) * mm});
            skLineSegment(sketch, "E365", {"start": v(-16.03, 17.15) * mm, "end": v(-16.02, 17.13) * mm});
            skLineSegment(sketch, "E366", {"start": v(-16.02, 17.13) * mm, "end": v(-16, 17.12) * mm});
            skLineSegment(sketch, "E367", {"start": v(-16, 17.12) * mm, "end": v(-14.42, 15.44) * mm});
            skLineSegment(sketch, "E368", {"start": v(-14.42, 15.44) * mm, "end": v(-16.96, 12.54) * mm});
            skLineSegment(sketch, "E369", {"start": v(-16.96, 12.54) * mm, "end": v(-18.83, 13.9) * mm});
            skLineSegment(sketch, "E370", {"start": v(-18.83, 13.9) * mm, "end": v(-18.85, 13.9) * mm});
            skLineSegment(sketch, "E371", {"start": v(-18.85, 13.9) * mm, "end": v(-18.87, 13.92) * mm});
            skLineSegment(sketch, "E372", {"start": v(-18.87, 13.92) * mm, "end": v(-18.9, 13.94) * mm});
            skLineSegment(sketch, "E373", {"start": v(-18.9, 13.94) * mm, "end": v(-18.95, 13.97) * mm});
            skLineSegment(sketch, "E374", {"start": v(-18.95, 13.97) * mm, "end": v(-19.01, 14) * mm});
            skLineSegment(sketch, "E375", {"start": v(-19.01, 14) * mm, "end": v(-19.08, 14.04) * mm});
            skLineSegment(sketch, "E376", {"start": v(-19.08, 14.04) * mm, "end": v(-19.16, 14.08) * mm});
            skLineSegment(sketch, "E377", {"start": v(-19.16, 14.08) * mm, "end": v(-19.26, 14.12) * mm});
            skLineSegment(sketch, "E378", {"start": v(-19.26, 14.12) * mm, "end": v(-19.36, 14.17) * mm});
            skLineSegment(sketch, "E379", {"start": v(-19.36, 14.17) * mm, "end": v(-19.48, 14.22) * mm});
            skLineSegment(sketch, "E380", {"start": v(-19.48, 14.22) * mm, "end": v(-19.62, 14.27) * mm});
            skLineSegment(sketch, "E381", {"start": v(-19.62, 14.27) * mm, "end": v(-19.76, 14.32) * mm});
            skLineSegment(sketch, "E382", {"start": v(-19.76, 14.32) * mm, "end": v(-19.92, 14.37) * mm});
            skLineSegment(sketch, "E383", {"start": v(-19.92, 14.37) * mm, "end": v(-20.1, 14.42) * mm});
            skLineSegment(sketch, "E384", {"start": v(-20.1, 14.42) * mm, "end": v(-20.28, 14.48) * mm});
            skLineSegment(sketch, "E385", {"start": v(-20.28, 14.48) * mm, "end": v(-20.48, 14.53) * mm});
            skLineSegment(sketch, "E386", {"start": v(-20.48, 14.53) * mm, "end": v(-20.69, 14.58) * mm});
            skLineSegment(sketch, "E387", {"start": v(-20.69, 14.58) * mm, "end": v(-20.91, 14.62) * mm});
            skLineSegment(sketch, "E388", {"start": v(-20.91, 14.62) * mm, "end": v(-21.15, 14.67) * mm});
            skLineSegment(sketch, "E389", {"start": v(-21.15, 14.67) * mm, "end": v(-21.4, 14.7) * mm});
            skLineSegment(sketch, "E390", {"start": v(-21.4, 14.7) * mm, "end": v(-21.67, 14.74) * mm});
            skLineSegment(sketch, "E391", {"start": v(-21.67, 14.74) * mm, "end": v(-21.95, 14.77) * mm});
            skLineSegment(sketch, "E392", {"start": v(-21.95, 14.77) * mm, "end": v(-22.24, 14.8) * mm});
            skLineSegment(sketch, "E393", {"start": v(-22.24, 14.8) * mm, "end": v(-22.55, 14.82) * mm});
            skLineSegment(sketch, "E394", {"start": v(-22.55, 14.82) * mm, "end": v(-22.87, 14.83) * mm});
            skLineSegment(sketch, "E395", {"start": v(-22.87, 14.83) * mm, "end": v(-23.2, 14.84) * mm});
            skLineSegment(sketch, "E396", {"start": v(-23.2, 14.84) * mm, "end": v(-23.54, 14.83) * mm});
            skLineSegment(sketch, "E397", {"start": v(-23.54, 14.83) * mm, "end": v(-23.9, 14.82) * mm});
            skLineSegment(sketch, "E398", {"start": v(-23.9, 14.82) * mm, "end": v(-24.06, 14.68) * mm});
            skLineSegment(sketch, "E399", {"start": v(-24.06, 14.68) * mm, "end": v(-24.9, 13.18) * mm});
            skLineSegment(sketch, "E400", {"start": v(-24.9, 13.18) * mm, "end": v(-24.94, 12.97) * mm});
            skLineSegment(sketch, "E401", {"start": v(-24.94, 12.97) * mm, "end": v(-24.76, 12.66) * mm});
            skLineSegment(sketch, "E402", {"start": v(-24.76, 12.66) * mm, "end": v(-24.58, 12.37) * mm});
            skLineSegment(sketch, "E403", {"start": v(-24.58, 12.37) * mm, "end": v(-24.4, 12.09) * mm});
            skLineSegment(sketch, "E404", {"start": v(-24.4, 12.09) * mm, "end": v(-24.23, 11.82) * mm});
            skLineSegment(sketch, "E405", {"start": v(-24.23, 11.82) * mm, "end": v(-24.05, 11.57) * mm});
            skLineSegment(sketch, "E406", {"start": v(-24.05, 11.57) * mm, "end": v(-23.88, 11.33) * mm});
            skLineSegment(sketch, "E407", {"start": v(-23.88, 11.33) * mm, "end": v(-23.7, 11.11) * mm});
            skLineSegment(sketch, "E408", {"start": v(-23.7, 11.11) * mm, "end": v(-23.54, 10.9) * mm});
            skLineSegment(sketch, "E409", {"start": v(-23.54, 10.9) * mm, "end": v(-23.37, 10.7) * mm});
            skLineSegment(sketch, "E410", {"start": v(-23.37, 10.7) * mm, "end": v(-23.2, 10.53) * mm});
            skLineSegment(sketch, "E411", {"start": v(-23.2, 10.53) * mm, "end": v(-23.05, 10.36) * mm});
            skLineSegment(sketch, "E412", {"start": v(-23.05, 10.36) * mm, "end": v(-22.9, 10.2) * mm});
            skLineSegment(sketch, "E413", {"start": v(-22.9, 10.2) * mm, "end": v(-22.75, 10.06) * mm});
            skLineSegment(sketch, "E414", {"start": v(-22.75, 10.06) * mm, "end": v(-22.61, 9.93) * mm});
            skLineSegment(sketch, "E415", {"start": v(-22.61, 9.93) * mm, "end": v(-22.48, 9.81) * mm});
            skLineSegment(sketch, "E416", {"start": v(-22.48, 9.81) * mm, "end": v(-22.35, 9.7) * mm});
            skLineSegment(sketch, "E417", {"start": v(-22.35, 9.7) * mm, "end": v(-22.23, 9.6) * mm});
            skLineSegment(sketch, "E418", {"start": v(-22.23, 9.6) * mm, "end": v(-22.12, 9.52) * mm});
            skLineSegment(sketch, "E419", {"start": v(-22.12, 9.52) * mm, "end": v(-22.01, 9.44) * mm});
            skLineSegment(sketch, "E420", {"start": v(-22.01, 9.44) * mm, "end": v(-21.92, 9.38) * mm});
            skLineSegment(sketch, "E421", {"start": v(-21.92, 9.38) * mm, "end": v(-21.83, 9.32) * mm});
            skLineSegment(sketch, "E422", {"start": v(-21.83, 9.32) * mm, "end": v(-21.75, 9.27) * mm});
            skLineSegment(sketch, "E423", {"start": v(-21.75, 9.27) * mm, "end": v(-21.68, 9.23) * mm});
            skLineSegment(sketch, "E424", {"start": v(-21.68, 9.23) * mm, "end": v(-21.63, 9.2) * mm});
            skLineSegment(sketch, "E425", {"start": v(-21.63, 9.2) * mm, "end": v(-21.58, 9.17) * mm});
            skLineSegment(sketch, "E426", {"start": v(-21.58, 9.17) * mm, "end": v(-21.54, 9.15) * mm});
            skLineSegment(sketch, "E427", {"start": v(-21.54, 9.15) * mm, "end": v(-21.52, 9.14) * mm});
            skLineSegment(sketch, "E428", {"start": v(-21.52, 9.14) * mm, "end": v(-21.5, 9.13) * mm});
            skLineSegment(sketch, "E429", {"start": v(-21.5, 9.13) * mm, "end": v(-19.37, 8.25) * mm});
            skLineSegment(sketch, "E430", {"start": v(-19.37, 8.25) * mm, "end": v(-20.52, 4.56) * mm});
            skLineSegment(sketch, "E431", {"start": v(-20.52, 4.56) * mm, "end": v(-22.78, 5.04) * mm});
            skLineSegment(sketch, "E432", {"start": v(-22.78, 5.04) * mm, "end": v(-22.8, 5.04) * mm});
            skLineSegment(sketch, "E433", {"start": v(-22.8, 5.04) * mm, "end": v(-22.82, 5.04) * mm});
            skLineSegment(sketch, "E434", {"start": v(-22.82, 5.04) * mm, "end": v(-22.86, 5.05) * mm});
            skLineSegment(sketch, "E435", {"start": v(-22.86, 5.05) * mm, "end": v(-22.91, 5.06) * mm});
            skLineSegment(sketch, "E436", {"start": v(-22.91, 5.06) * mm, "end": v(-22.98, 5.06) * mm});
            skLineSegment(sketch, "E437", {"start": v(-22.98, 5.06) * mm, "end": v(-23.06, 5.07) * mm});
            skLineSegment(sketch, "E438", {"start": v(-23.06, 5.07) * mm, "end": v(-23.15, 5.07) * mm});
            skLineSegment(sketch, "E439", {"start": v(-23.15, 5.07) * mm, "end": v(-23.25, 5.07) * mm});
            skLineSegment(sketch, "E440", {"start": v(-23.25, 5.07) * mm, "end": v(-23.37, 5.07) * mm});
            skLineSegment(sketch, "E441", {"start": v(-23.37, 5.07) * mm, "end": v(-23.5, 5.07) * mm});
            skLineSegment(sketch, "E442", {"start": v(-23.5, 5.07) * mm, "end": v(-23.64, 5.06) * mm});
            skLineSegment(sketch, "E443", {"start": v(-23.64, 5.06) * mm, "end": v(-23.8, 5.05) * mm});
            skLineSegment(sketch, "E444", {"start": v(-23.8, 5.05) * mm, "end": v(-23.96, 5.03) * mm});
            skLineSegment(sketch, "E445", {"start": v(-23.96, 5.03) * mm, "end": v(-24.14, 5.01) * mm});
            skLineSegment(sketch, "E446", {"start": v(-24.14, 5.01) * mm, "end": v(-24.33, 4.98) * mm});
            skLineSegment(sketch, "E447", {"start": v(-24.33, 4.98) * mm, "end": v(-24.53, 4.95) * mm});
            skLineSegment(sketch, "E448", {"start": v(-24.53, 4.95) * mm, "end": v(-24.75, 4.9) * mm});
            skLineSegment(sketch, "E449", {"start": v(-24.75, 4.9) * mm, "end": v(-24.97, 4.86) * mm});
            skLineSegment(sketch, "E450", {"start": v(-24.97, 4.86) * mm, "end": v(-25.2, 4.8) * mm});
            skLineSegment(sketch, "E451", {"start": v(-25.2, 4.8) * mm, "end": v(-25.46, 4.73) * mm});
            skLineSegment(sketch, "E452", {"start": v(-25.46, 4.73) * mm, "end": v(-25.71, 4.66) * mm});
            skLineSegment(sketch, "E453", {"start": v(-25.71, 4.66) * mm, "end": v(-25.98, 4.57) * mm});
            skLineSegment(sketch, "E454", {"start": v(-25.98, 4.57) * mm, "end": v(-26.26, 4.48) * mm});
            skLineSegment(sketch, "E455", {"start": v(-26.26, 4.48) * mm, "end": v(-26.55, 4.37) * mm});
            skLineSegment(sketch, "E456", {"start": v(-26.55, 4.37) * mm, "end": v(-26.84, 4.25) * mm});
            skLineSegment(sketch, "E457", {"start": v(-26.84, 4.25) * mm, "end": v(-27.15, 4.12) * mm});
            skLineSegment(sketch, "E458", {"start": v(-27.15, 4.12) * mm, "end": v(-27.46, 3.98) * mm});
            skLineSegment(sketch, "E459", {"start": v(-27.46, 3.98) * mm, "end": v(-27.78, 3.83) * mm});
            skLineSegment(sketch, "E460", {"start": v(-27.78, 3.83) * mm, "end": v(-27.88, 3.63) * mm});
            skLineSegment(sketch, "E461", {"start": v(-27.88, 3.63) * mm, "end": v(-28.03, 1.92) * mm});
            skLineSegment(sketch, "E462", {"start": v(-28.03, 1.92) * mm, "end": v(-27.98, 1.71) * mm});
            skLineSegment(sketch, "E463", {"start": v(-27.98, 1.71) * mm, "end": v(-27.69, 1.5) * mm});
            skLineSegment(sketch, "E464", {"start": v(-27.69, 1.5) * mm, "end": v(-27.4, 1.3) * mm});
            skLineSegment(sketch, "E465", {"start": v(-27.4, 1.3) * mm, "end": v(-27.13, 1.12) * mm});
            skLineSegment(sketch, "E466", {"start": v(-27.13, 1.12) * mm, "end": v(-26.86, 0.95) * mm});
            skLineSegment(sketch, "E467", {"start": v(-26.86, 0.95) * mm, "end": v(-26.6, 0.8) * mm});
            skLineSegment(sketch, "E468", {"start": v(-26.6, 0.8) * mm, "end": v(-26.34, 0.65) * mm});
            skLineSegment(sketch, "E469", {"start": v(-26.34, 0.65) * mm, "end": v(-26.1, 0.52) * mm});
            skLineSegment(sketch, "E470", {"start": v(-26.1, 0.52) * mm, "end": v(-25.86, 0.4) * mm});
            skLineSegment(sketch, "E471", {"start": v(-25.86, 0.4) * mm, "end": v(-25.63, 0.28) * mm});
            skLineSegment(sketch, "E472", {"start": v(-25.63, 0.28) * mm, "end": v(-25.4, 0.18) * mm});
            skLineSegment(sketch, "E473", {"start": v(-25.4, 0.18) * mm, "end": v(-25.2, 0.1) * mm});
            skLineSegment(sketch, "E474", {"start": v(-25.2, 0.1) * mm, "end": v(-25, 0.01) * mm});
            skLineSegment(sketch, "E475", {"start": v(-25, 0.01) * mm, "end": v(-24.8, -0.06) * mm});
            skLineSegment(sketch, "E476", {"start": v(-24.8, -0.06) * mm, "end": v(-24.62, -0.12) * mm});
            skLineSegment(sketch, "E477", {"start": v(-24.62, -0.12) * mm, "end": v(-24.44, -0.17) * mm});
            skLineSegment(sketch, "E478", {"start": v(-24.44, -0.17) * mm, "end": v(-24.28, -0.22) * mm});
            skLineSegment(sketch, "E479", {"start": v(-24.28, -0.22) * mm, "end": v(-24.13, -0.26) * mm});
            skLineSegment(sketch, "E480", {"start": v(-24.13, -0.26) * mm, "end": v(-24, -0.3) * mm});
            skLineSegment(sketch, "E481", {"start": v(-24, -0.3) * mm, "end": v(-23.87, -0.32) * mm});
            skLineSegment(sketch, "E482", {"start": v(-23.87, -0.32) * mm, "end": v(-23.75, -0.34) * mm});
            skLineSegment(sketch, "E483", {"start": v(-23.75, -0.34) * mm, "end": v(-23.65, -0.36) * mm});
            skLineSegment(sketch, "E484", {"start": v(-23.65, -0.36) * mm, "end": v(-23.56, -0.37) * mm});
            skLineSegment(sketch, "E485", {"start": v(-23.56, -0.37) * mm, "end": v(-23.48, -0.38) * mm});
            skLineSegment(sketch, "E486", {"start": v(-23.48, -0.38) * mm, "end": v(-23.42, -0.39) * mm});
            skLineSegment(sketch, "E487", {"start": v(-23.42, -0.39) * mm, "end": v(-23.36, -0.4) * mm});
            skLineSegment(sketch, "E488", {"start": v(-23.36, -0.4) * mm, "end": v(-23.32, -0.4) * mm});
            skLineSegment(sketch, "E489", {"start": v(-23.32, -0.4) * mm, "end": v(-23.28, -0.4) * mm});
            skLineSegment(sketch, "E490", {"start": v(-23.28, -0.4) * mm, "end": v(-20.97, -0.34) * mm});
            skLineSegment(sketch, "E491", {"start": v(-20.97, -0.34) * mm, "end": v(-20.52, -4.18) * mm});
            skLineSegment(sketch, "E492", {"start": v(-20.52, -4.18) * mm, "end": v(-22.78, -4.66) * mm});
            skLineSegment(sketch, "E493", {"start": v(-22.78, -4.66) * mm, "end": v(-22.8, -4.66) * mm});
            skLineSegment(sketch, "E494", {"start": v(-22.8, -4.66) * mm, "end": v(-22.82, -4.67) * mm});
            skLineSegment(sketch, "E495", {"start": v(-22.82, -4.67) * mm, "end": v(-22.86, -4.68) * mm});
            skLineSegment(sketch, "E496", {"start": v(-22.86, -4.68) * mm, "end": v(-22.9, -4.7) * mm});
            skLineSegment(sketch, "E497", {"start": v(-22.9, -4.7) * mm, "end": v(-22.97, -4.72) * mm});
            skLineSegment(sketch, "E498", {"start": v(-22.97, -4.72) * mm, "end": v(-23.05, -4.74) * mm});
            skLineSegment(sketch, "E499", {"start": v(-23.05, -4.74) * mm, "end": v(-23.13, -4.78) * mm});
            skLineSegment(sketch, "E500", {"start": v(-23.13, -4.78) * mm, "end": v(-23.23, -4.82) * mm});
            skLineSegment(sketch, "E501", {"start": v(-23.23, -4.82) * mm, "end": v(-23.33, -4.87) * mm});
            skLineSegment(sketch, "E502", {"start": v(-23.33, -4.87) * mm, "end": v(-23.45, -4.92) * mm});
            skLineSegment(sketch, "E503", {"start": v(-23.45, -4.92) * mm, "end": v(-23.58, -4.99) * mm});
            skLineSegment(sketch, "E504", {"start": v(-23.58, -4.99) * mm, "end": v(-23.71, -5.06) * mm});
            skLineSegment(sketch, "E505", {"start": v(-23.71, -5.06) * mm, "end": v(-23.86, -5.14) * mm});
            skLineSegment(sketch, "E506", {"start": v(-23.86, -5.14) * mm, "end": v(-24.01, -5.24) * mm});
            skLineSegment(sketch, "E507", {"start": v(-24.01, -5.24) * mm, "end": v(-24.17, -5.34) * mm});
            skLineSegment(sketch, "E508", {"start": v(-24.17, -5.34) * mm, "end": v(-24.35, -5.45) * mm});
            skLineSegment(sketch, "E509", {"start": v(-24.35, -5.45) * mm, "end": v(-24.52, -5.58) * mm});
            skLineSegment(sketch, "E510", {"start": v(-24.52, -5.58) * mm, "end": v(-24.7, -5.71) * mm});
            skLineSegment(sketch, "E511", {"start": v(-24.7, -5.71) * mm, "end": v(-24.9, -5.86) * mm});
            skLineSegment(sketch, "E512", {"start": v(-24.9, -5.86) * mm, "end": v(-25.1, -6.02) * mm});
            skLineSegment(sketch, "E513", {"start": v(-25.1, -6.02) * mm, "end": v(-25.3, -6.2) * mm});
            skLineSegment(sketch, "E514", {"start": v(-25.3, -6.2) * mm, "end": v(-25.51, -6.38) * mm});
            skLineSegment(sketch, "E515", {"start": v(-25.51, -6.38) * mm, "end": v(-25.73, -6.58) * mm});
            skLineSegment(sketch, "E516", {"start": v(-25.73, -6.58) * mm, "end": v(-25.95, -6.8) * mm});
            skLineSegment(sketch, "E517", {"start": v(-25.95, -6.8) * mm, "end": v(-26.17, -7.03) * mm});
            skLineSegment(sketch, "E518", {"start": v(-26.17, -7.03) * mm, "end": v(-26.4, -7.27) * mm});
            skLineSegment(sketch, "E519", {"start": v(-26.4, -7.27) * mm, "end": v(-26.63, -7.52) * mm});
            skLineSegment(sketch, "E520", {"start": v(-26.63, -7.52) * mm, "end": v(-26.86, -7.8) * mm});
            skLineSegment(sketch, "E521", {"start": v(-26.86, -7.8) * mm, "end": v(-26.86, -8.01) * mm});
            skLineSegment(sketch, "E522", {"start": v(-26.86, -8.01) * mm, "end": v(-26.31, -9.64) * mm});
            skLineSegment(sketch, "E523", {"start": v(-26.31, -9.64) * mm, "end": v(-26.17, -9.81) * mm});
            skLineSegment(sketch, "E524", {"start": v(-26.17, -9.81) * mm, "end": v(-25.83, -9.89) * mm});
            skLineSegment(sketch, "E525", {"start": v(-25.83, -9.89) * mm, "end": v(-25.49, -9.95) * mm});
            skLineSegment(sketch, "E526", {"start": v(-25.49, -9.95) * mm, "end": v(-25.16, -10) * mm});
            skLineSegment(sketch, "E527", {"start": v(-25.16, -10) * mm, "end": v(-24.85, -10.05) * mm});
            skLineSegment(sketch, "E528", {"start": v(-24.85, -10.05) * mm, "end": v(-24.54, -10.09) * mm});
            skLineSegment(sketch, "E529", {"start": v(-24.54, -10.09) * mm, "end": v(-24.25, -10.12) * mm});
            skLineSegment(sketch, "E530", {"start": v(-24.25, -10.12) * mm, "end": v(-23.97, -10.14) * mm});
            skLineSegment(sketch, "E531", {"start": v(-23.97, -10.14) * mm, "end": v(-23.7, -10.15) * mm});
            skLineSegment(sketch, "E532", {"start": v(-23.7, -10.15) * mm, "end": v(-23.45, -10.16) * mm});
            skLineSegment(sketch, "E533", {"start": v(-23.45, -10.16) * mm, "end": v(-23.2, -10.16) * mm});
            skLineSegment(sketch, "E534", {"start": v(-23.2, -10.16) * mm, "end": v(-22.97, -10.15) * mm});
            skLineSegment(sketch, "E535", {"start": v(-22.97, -10.15) * mm, "end": v(-22.76, -10.15) * mm});
            skLineSegment(sketch, "E536", {"start": v(-22.76, -10.15) * mm, "end": v(-22.55, -10.13) * mm});
            skLineSegment(sketch, "E537", {"start": v(-22.55, -10.13) * mm, "end": v(-22.36, -10.11) * mm});
            skLineSegment(sketch, "E538", {"start": v(-22.36, -10.11) * mm, "end": v(-22.18, -10.1) * mm});
            skLineSegment(sketch, "E539", {"start": v(-22.18, -10.1) * mm, "end": v(-22.01, -10.07) * mm});
            skLineSegment(sketch, "E540", {"start": v(-22.01, -10.07) * mm, "end": v(-21.86, -10.05) * mm});
            skLineSegment(sketch, "E541", {"start": v(-21.86, -10.05) * mm, "end": v(-21.72, -10.02) * mm});
            skLineSegment(sketch, "E542", {"start": v(-21.72, -10.02) * mm, "end": v(-21.6, -10) * mm});
            skLineSegment(sketch, "E543", {"start": v(-21.6, -10) * mm, "end": v(-21.48, -9.97) * mm});
            skLineSegment(sketch, "E544", {"start": v(-21.48, -9.97) * mm, "end": v(-21.38, -9.94) * mm});
            skLineSegment(sketch, "E545", {"start": v(-21.38, -9.94) * mm, "end": v(-21.3, -9.92) * mm});
            skLineSegment(sketch, "E546", {"start": v(-21.3, -9.92) * mm, "end": v(-21.22, -9.9) * mm});
            skLineSegment(sketch, "E547", {"start": v(-21.22, -9.9) * mm, "end": v(-21.15, -9.87) * mm});
            skLineSegment(sketch, "E548", {"start": v(-21.15, -9.87) * mm, "end": v(-21.1, -9.86) * mm});
            skLineSegment(sketch, "E549", {"start": v(-21.1, -9.86) * mm, "end": v(-21.07, -9.84) * mm});
            skLineSegment(sketch, "E550", {"start": v(-21.07, -9.84) * mm, "end": v(-21.04, -9.83) * mm});
            skLineSegment(sketch, "E551", {"start": v(-21.04, -9.83) * mm, "end": v(-21.02, -9.82) * mm});
            skLineSegment(sketch, "E552", {"start": v(-21.02, -9.82) * mm, "end": v(-18.94, -8.83) * mm});
            skLineSegment(sketch, "E553", {"start": v(-18.94, -8.83) * mm, "end": v(-16.96, -12.15) * mm});
            skLineSegment(sketch, "E554", {"start": v(-16.96, -12.15) * mm, "end": v(-18.83, -13.51) * mm});
            skLineSegment(sketch, "E555", {"start": v(-18.83, -13.51) * mm, "end": v(-18.85, -13.52) * mm});
            skLineSegment(sketch, "E556", {"start": v(-18.85, -13.52) * mm, "end": v(-18.87, -13.54) * mm});
            skLineSegment(sketch, "E557", {"start": v(-18.87, -13.54) * mm, "end": v(-18.9, -13.57) * mm});
            skLineSegment(sketch, "E558", {"start": v(-18.9, -13.57) * mm, "end": v(-18.94, -13.6) * mm});
            skLineSegment(sketch, "E559", {"start": v(-18.94, -13.6) * mm, "end": v(-18.99, -13.65) * mm});
            skLineSegment(sketch, "E560", {"start": v(-18.99, -13.65) * mm, "end": v(-19.04, -13.7) * mm});
            skLineSegment(sketch, "E561", {"start": v(-19.04, -13.7) * mm, "end": v(-19.1, -13.77) * mm});
            skLineSegment(sketch, "E562", {"start": v(-19.1, -13.77) * mm, "end": v(-19.18, -13.84) * mm});
            skLineSegment(sketch, "E563", {"start": v(-19.18, -13.84) * mm, "end": v(-19.26, -13.93) * mm});
            skLineSegment(sketch, "E564", {"start": v(-19.26, -13.93) * mm, "end": v(-19.34, -14.03) * mm});
            skLineSegment(sketch, "E565", {"start": v(-19.34, -14.03) * mm, "end": v(-19.43, -14.14) * mm});
            skLineSegment(sketch, "E566", {"start": v(-19.43, -14.14) * mm, "end": v(-19.52, -14.26) * mm});
            skLineSegment(sketch, "E567", {"start": v(-19.52, -14.26) * mm, "end": v(-19.62, -14.4) * mm});
            skLineSegment(sketch, "E568", {"start": v(-19.62, -14.4) * mm, "end": v(-19.73, -14.54) * mm});
            skLineSegment(sketch, "E569", {"start": v(-19.73, -14.54) * mm, "end": v(-19.83, -14.7) * mm});
            skLineSegment(sketch, "E570", {"start": v(-19.83, -14.7) * mm, "end": v(-19.94, -14.88) * mm});
            skLineSegment(sketch, "E571", {"start": v(-19.94, -14.88) * mm, "end": v(-20.06, -15.06) * mm});
            skLineSegment(sketch, "E572", {"start": v(-20.06, -15.06) * mm, "end": v(-20.17, -15.26) * mm});
            skLineSegment(sketch, "E573", {"start": v(-20.17, -15.26) * mm, "end": v(-20.28, -15.48) * mm});
            skLineSegment(sketch, "E574", {"start": v(-20.28, -15.48) * mm, "end": v(-20.4, -15.7) * mm});
            skLineSegment(sketch, "E575", {"start": v(-20.4, -15.7) * mm, "end": v(-20.52, -15.95) * mm});
            skLineSegment(sketch, "E576", {"start": v(-20.52, -15.95) * mm, "end": v(-20.63, -16.2) * mm});
            skLineSegment(sketch, "E577", {"start": v(-20.63, -16.2) * mm, "end": v(-20.75, -16.47) * mm});
            skLineSegment(sketch, "E578", {"start": v(-20.75, -16.47) * mm, "end": v(-20.86, -16.76) * mm});
            skLineSegment(sketch, "E579", {"start": v(-20.86, -16.76) * mm, "end": v(-20.97, -17.06) * mm});
            skLineSegment(sketch, "E580", {"start": v(-20.97, -17.06) * mm, "end": v(-21.08, -17.37) * mm});
            skLineSegment(sketch, "E581", {"start": v(-21.08, -17.37) * mm, "end": v(-21.18, -17.7) * mm});
            skLineSegment(sketch, "E582", {"start": v(-21.18, -17.7) * mm, "end": v(-21.28, -18.04) * mm});
            skLineSegment(sketch, "E583", {"start": v(-21.28, -18.04) * mm, "end": v(-21.2, -18.24) * mm});
            skLineSegment(sketch, "E584", {"start": v(-21.2, -18.24) * mm, "end": v(-20.03, -19.5) * mm});
            skLineSegment(sketch, "E585", {"start": v(-20.03, -19.5) * mm, "end": v(-19.84, -19.6) * mm});
            skLineSegment(sketch, "E586", {"start": v(-19.84, -19.6) * mm, "end": v(-19.5, -19.53) * mm});
            skLineSegment(sketch, "E587", {"start": v(-19.5, -19.53) * mm, "end": v(-19.16, -19.45) * mm});
            skLineSegment(sketch, "E588", {"start": v(-19.16, -19.45) * mm, "end": v(-18.84, -19.37) * mm});
            skLineSegment(sketch, "E589", {"start": v(-18.84, -19.37) * mm, "end": v(-18.53, -19.28) * mm});
            skLineSegment(sketch, "E590", {"start": v(-18.53, -19.28) * mm, "end": v(-18.24, -19.2) * mm});
            skLineSegment(sketch, "E591", {"start": v(-18.24, -19.2) * mm, "end": v(-17.96, -19.1) * mm});
            skLineSegment(sketch, "E592", {"start": v(-17.96, -19.1) * mm, "end": v(-17.7, -19) * mm});
            skLineSegment(sketch, "E593", {"start": v(-17.7, -19) * mm, "end": v(-17.44, -18.9) * mm});
            skLineSegment(sketch, "E594", {"start": v(-17.44, -18.9) * mm, "end": v(-17.2, -18.81) * mm});
            skLineSegment(sketch, "E595", {"start": v(-17.2, -18.81) * mm, "end": v(-16.98, -18.71) * mm});
            skLineSegment(sketch, "E596", {"start": v(-16.98, -18.71) * mm, "end": v(-16.78, -18.61) * mm});
            skLineSegment(sketch, "E597", {"start": v(-16.78, -18.61) * mm, "end": v(-16.58, -18.52) * mm});
            skLineSegment(sketch, "E598", {"start": v(-16.58, -18.52) * mm, "end": v(-16.4, -18.42) * mm});
            skLineSegment(sketch, "E599", {"start": v(-16.4, -18.42) * mm, "end": v(-16.23, -18.33) * mm});
            skLineSegment(sketch, "E600", {"start": v(-16.23, -18.33) * mm, "end": v(-16.08, -18.24) * mm});
            skLineSegment(sketch, "E601", {"start": v(-16.08, -18.24) * mm, "end": v(-15.93, -18.15) * mm});
            skLineSegment(sketch, "E602", {"start": v(-15.93, -18.15) * mm, "end": v(-15.8, -18.06) * mm});
            skLineSegment(sketch, "E603", {"start": v(-15.8, -18.06) * mm, "end": v(-15.69, -17.98) * mm});
            skLineSegment(sketch, "E604", {"start": v(-15.69, -17.98) * mm, "end": v(-15.58, -17.9) * mm});
            skLineSegment(sketch, "E605", {"start": v(-15.58, -17.9) * mm, "end": v(-15.49, -17.84) * mm});
            skLineSegment(sketch, "E606", {"start": v(-15.49, -17.84) * mm, "end": v(-15.4, -17.77) * mm});
            skLineSegment(sketch, "E607", {"start": v(-15.4, -17.77) * mm, "end": v(-15.34, -17.72) * mm});
            skLineSegment(sketch, "E608", {"start": v(-15.34, -17.72) * mm, "end": v(-15.28, -17.66) * mm});
            skLineSegment(sketch, "E609", {"start": v(-15.28, -17.66) * mm, "end": v(-15.23, -17.62) * mm});
            skLineSegment(sketch, "E610", {"start": v(-15.23, -17.62) * mm, "end": v(-15.2, -17.58) * mm});
            skLineSegment(sketch, "E611", {"start": v(-15.2, -17.58) * mm, "end": v(-15.16, -17.55) * mm});
            skLineSegment(sketch, "E612", {"start": v(-15.16, -17.55) * mm, "end": v(-15.14, -17.53) * mm});
            skLineSegment(sketch, "E613", {"start": v(-15.14, -17.53) * mm, "end": v(-15.13, -17.52) * mm});
            skLineSegment(sketch, "E614", {"start": v(-15.13, -17.52) * mm, "end": v(-13.63, -15.76) * mm});
            skLineSegment(sketch, "E615", {"start": v(-13.63, -15.76) * mm, "end": v(-10.47, -18) * mm});
            skLineSegment(sketch, "E616", {"start": v(-10.47, -18) * mm, "end": v(-11.63, -20) * mm});
            skLineSegment(sketch, "E617", {"start": v(-11.63, -20) * mm, "end": v(-11.65, -20.04) * mm});
            skLineSegment(sketch, "E618", {"start": v(-11.65, -20.04) * mm, "end": v(-11.67, -20.07) * mm});
            skLineSegment(sketch, "E619", {"start": v(-11.67, -20.07) * mm, "end": v(-11.69, -20.12) * mm});
            skLineSegment(sketch, "E620", {"start": v(-11.69, -20.12) * mm, "end": v(-11.72, -20.18) * mm});
            skLineSegment(sketch, "E621", {"start": v(-11.72, -20.18) * mm, "end": v(-11.75, -20.26) * mm});
            skLineSegment(sketch, "E622", {"start": v(-11.75, -20.26) * mm, "end": v(-11.78, -20.34) * mm});
            skLineSegment(sketch, "E623", {"start": v(-11.78, -20.34) * mm, "end": v(-11.81, -20.44) * mm});
            skLineSegment(sketch, "E624", {"start": v(-11.81, -20.44) * mm, "end": v(-11.85, -20.55) * mm});
            skLineSegment(sketch, "E625", {"start": v(-11.85, -20.55) * mm, "end": v(-11.88, -20.68) * mm});
            skLineSegment(sketch, "E626", {"start": v(-11.88, -20.68) * mm, "end": v(-11.92, -20.81) * mm});
            skLineSegment(sketch, "E627", {"start": v(-11.92, -20.81) * mm, "end": v(-11.96, -20.96) * mm});
            skLineSegment(sketch, "E628", {"start": v(-11.96, -20.96) * mm, "end": v(-12, -21.13) * mm});
            skLineSegment(sketch, "E629", {"start": v(-12, -21.13) * mm, "end": v(-12.03, -21.3) * mm});
            skLineSegment(sketch, "E630", {"start": v(-12.03, -21.3) * mm, "end": v(-12.06, -21.5) * mm});
            skLineSegment(sketch, "E631", {"start": v(-12.06, -21.5) * mm, "end": v(-12.09, -21.7) * mm});
            skLineSegment(sketch, "E632", {"start": v(-12.09, -21.7) * mm, "end": v(-12.11, -21.91) * mm});
            skLineSegment(sketch, "E633", {"start": v(-12.11, -21.91) * mm, "end": v(-12.14, -22.14) * mm});
            skLineSegment(sketch, "E634", {"start": v(-12.14, -22.14) * mm, "end": v(-12.16, -22.38) * mm});
            skLineSegment(sketch, "E635", {"start": v(-12.16, -22.38) * mm, "end": v(-12.17, -22.64) * mm});
            skLineSegment(sketch, "E636", {"start": v(-12.17, -22.64) * mm, "end": v(-12.18, -22.9) * mm});
            skLineSegment(sketch, "E637", {"start": v(-12.18, -22.9) * mm, "end": v(-12.18, -23.19) * mm});
            skLineSegment(sketch, "E638", {"start": v(-12.18, -23.19) * mm, "end": v(-12.17, -23.48) * mm});
            skLineSegment(sketch, "E639", {"start": v(-12.17, -23.48) * mm, "end": v(-12.16, -23.79) * mm});
            skLineSegment(sketch, "E640", {"start": v(-12.16, -23.79) * mm, "end": v(-12.14, -24.1) * mm});
            skLineSegment(sketch, "E641", {"start": v(-12.14, -24.1) * mm, "end": v(-12.11, -24.44) * mm});
            skLineSegment(sketch, "E642", {"start": v(-12.11, -24.44) * mm, "end": v(-12.07, -24.78) * mm});
            skLineSegment(sketch, "E643", {"start": v(-12.07, -24.78) * mm, "end": v(-12.03, -25.13) * mm});
            skLineSegment(sketch, "E644", {"start": v(-12.03, -25.13) * mm, "end": v(-11.87, -25.28) * mm});
            skLineSegment(sketch, "E645", {"start": v(-11.87, -25.28) * mm, "end": v(-10.29, -25.96) * mm});
            skLineSegment(sketch, "E646", {"start": v(-10.29, -25.96) * mm, "end": v(-10.07, -25.97) * mm});
            skLineSegment(sketch, "E647", {"start": v(-10.07, -25.97) * mm, "end": v(-9.78, -25.76) * mm});
            skLineSegment(sketch, "E648", {"start": v(-9.78, -25.76) * mm, "end": v(-9.5, -25.56) * mm});
            skLineSegment(sketch, "E649", {"start": v(-9.5, -25.56) * mm, "end": v(-9.25, -25.35) * mm});
            skLineSegment(sketch, "E650", {"start": v(-9.25, -25.35) * mm, "end": v(-9, -25.15) * mm});
            skLineSegment(sketch, "E651", {"start": v(-9, -25.15) * mm, "end": v(-8.77, -24.95) * mm});
            skLineSegment(sketch, "E652", {"start": v(-8.77, -24.95) * mm, "end": v(-8.56, -24.75) * mm});
            skLineSegment(sketch, "E653", {"start": v(-8.56, -24.75) * mm, "end": v(-8.35, -24.55) * mm});
            skLineSegment(sketch, "E654", {"start": v(-8.35, -24.55) * mm, "end": v(-8.16, -24.36) * mm});
            skLineSegment(sketch, "E655", {"start": v(-8.16, -24.36) * mm, "end": v(-7.99, -24.18) * mm});
            skLineSegment(sketch, "E656", {"start": v(-7.99, -24.18) * mm, "end": v(-7.83, -24) * mm});
            skLineSegment(sketch, "E657", {"start": v(-7.83, -24) * mm, "end": v(-7.67, -23.82) * mm});
            skLineSegment(sketch, "E658", {"start": v(-7.67, -23.82) * mm, "end": v(-7.54, -23.66) * mm});
            skLineSegment(sketch, "E659", {"start": v(-7.54, -23.66) * mm, "end": v(-7.4, -23.5) * mm});
            skLineSegment(sketch, "E660", {"start": v(-7.4, -23.5) * mm, "end": v(-7.3, -23.34) * mm});
            skLineSegment(sketch, "E661", {"start": v(-7.3, -23.34) * mm, "end": v(-7.19, -23.2) * mm});
            skLineSegment(sketch, "E662", {"start": v(-7.19, -23.2) * mm, "end": v(-7.1, -23.06) * mm});
            skLineSegment(sketch, "E663", {"start": v(-7.1, -23.06) * mm, "end": v(-7.01, -22.93) * mm});
            skLineSegment(sketch, "E664", {"start": v(-7.01, -22.93) * mm, "end": v(-6.94, -22.8) * mm});
            skLineSegment(sketch, "E665", {"start": v(-6.94, -22.8) * mm, "end": v(-6.87, -22.7) * mm});
            skLineSegment(sketch, "E666", {"start": v(-6.87, -22.7) * mm, "end": v(-6.81, -22.6) * mm});
            skLineSegment(sketch, "E667", {"start": v(-6.81, -22.6) * mm, "end": v(-6.77, -22.5) * mm});
            skLineSegment(sketch, "E668", {"start": v(-6.77, -22.5) * mm, "end": v(-6.73, -22.42) * mm});
            skLineSegment(sketch, "E669", {"start": v(-6.73, -22.42) * mm, "end": v(-6.7, -22.34) * mm});
            skLineSegment(sketch, "E670", {"start": v(-6.7, -22.34) * mm, "end": v(-6.67, -22.28) * mm});
            skLineSegment(sketch, "E671", {"start": v(-6.67, -22.28) * mm, "end": v(-6.65, -22.23) * mm});
            skLineSegment(sketch, "E672", {"start": v(-6.65, -22.23) * mm, "end": v(-6.63, -22.2) * mm});
            skLineSegment(sketch, "E673", {"start": v(-6.63, -22.2) * mm, "end": v(-6.62, -22.17) * mm});
            skLineSegment(sketch, "E674", {"start": v(-6.62, -22.17) * mm, "end": v(-6.62, -22.15) * mm});
            skLineSegment(sketch, "E675", {"start": v(-6.62, -22.15) * mm, "end": v(-5.96, -19.94) * mm});
            skLineSegment(sketch, "E676", {"start": v(-5.96, -19.94) * mm, "end": v(-2.17, -20.7) * mm});
            skLineSegment(sketch, "E677", {"start": v(-2.17, -20.7) * mm, "end": v(-2.41, -23) * mm});
            skLineSegment(sketch, "E678", {"start": v(-2.41, -23) * mm, "end": v(-2.41, -23) * mm});
            skLineSegment(sketch, "E679", {"start": v(-2.41, -23) * mm, "end": v(-2.41, -23.04) * mm});
            skLineSegment(sketch, "E680", {"start": v(-2.41, -23.04) * mm, "end": v(-2.41, -23.08) * mm});
            skLineSegment(sketch, "E681", {"start": v(-2.41, -23.08) * mm, "end": v(-2.41, -23.13) * mm});
            skLineSegment(sketch, "E682", {"start": v(-2.41, -23.13) * mm, "end": v(-2.41, -23.2) * mm});
            skLineSegment(sketch, "E683", {"start": v(-2.41, -23.2) * mm, "end": v(-2.41, -23.28) * mm});
            skLineSegment(sketch, "E684", {"start": v(-2.41, -23.28) * mm, "end": v(-2.4, -23.37) * mm});
            skLineSegment(sketch, "E685", {"start": v(-2.4, -23.37) * mm, "end": v(-2.4, -23.47) * mm});
            skLineSegment(sketch, "E686", {"start": v(-2.4, -23.47) * mm, "end": v(-2.38, -23.59) * mm});
            skLineSegment(sketch, "E687", {"start": v(-2.38, -23.59) * mm, "end": v(-2.36, -23.72) * mm});
            skLineSegment(sketch, "E688", {"start": v(-2.36, -23.72) * mm, "end": v(-2.34, -23.86) * mm});
            skLineSegment(sketch, "E689", {"start": v(-2.34, -23.86) * mm, "end": v(-2.32, -24) * mm});
            skLineSegment(sketch, "E690", {"start": v(-2.32, -24) * mm, "end": v(-2.28, -24.17) * mm});
            skLineSegment(sketch, "E691", {"start": v(-2.28, -24.17) * mm, "end": v(-2.24, -24.35) * mm});
            skLineSegment(sketch, "E692", {"start": v(-2.24, -24.35) * mm, "end": v(-2.2, -24.53) * mm});
            skLineSegment(sketch, "E693", {"start": v(-2.2, -24.53) * mm, "end": v(-2.14, -24.73) * mm});
            skLineSegment(sketch, "E694", {"start": v(-2.14, -24.73) * mm, "end": v(-2.07, -24.94) * mm});
            skLineSegment(sketch, "E695", {"start": v(-2.07, -24.94) * mm, "end": v(-2, -25.16) * mm});
            skLineSegment(sketch, "E696", {"start": v(-2, -25.16) * mm, "end": v(-1.92, -25.39) * mm});
            skLineSegment(sketch, "E697", {"start": v(-1.92, -25.39) * mm, "end": v(-1.83, -25.63) * mm});
            skLineSegment(sketch, "E698", {"start": v(-1.83, -25.63) * mm, "end": v(-1.73, -25.87) * mm});
            skLineSegment(sketch, "E699", {"start": v(-1.73, -25.87) * mm, "end": v(-1.61, -26.13) * mm});
            skLineSegment(sketch, "E700", {"start": v(-1.61, -26.13) * mm, "end": v(-1.49, -26.4) * mm});
            skLineSegment(sketch, "E701", {"start": v(-1.49, -26.4) * mm, "end": v(-1.35, -26.67) * mm});
            skLineSegment(sketch, "E702", {"start": v(-1.35, -26.67) * mm, "end": v(-1.2, -26.95) * mm});
            skLineSegment(sketch, "E703", {"start": v(-1.2, -26.95) * mm, "end": v(-1.04, -27.24) * mm});
            skLineSegment(sketch, "E704", {"start": v(-1.04, -27.24) * mm, "end": v(-0.87, -27.54) * mm});
            skLineSegment(sketch, "E705", {"start": v(-0.87, -27.54) * mm, "end": v(-0.68, -27.84) * mm});
            skLineSegment(sketch, "E706", {"start": v(-0.68, -27.84) * mm, "end": v(-0.48, -27.92) * mm});
            skLineSegment(sketch, "E707", {"start": v(-0.48, -27.92) * mm, "end": v(1.24, -27.9) * mm});
            skLineSegment(sketch, "E708", {"start": v(1.24, -27.9) * mm, "end": v(1.44, -27.82) * mm});
            skLineSegment(sketch, "E709", {"start": v(1.44, -27.82) * mm, "end": v(1.62, -27.5) * mm});
            skLineSegment(sketch, "E710", {"start": v(1.62, -27.5) * mm, "end": v(1.79, -27.2) * mm});
            skLineSegment(sketch, "E711", {"start": v(1.79, -27.2) * mm, "end": v(1.94, -26.91) * mm});
            skLineSegment(sketch, "E712", {"start": v(1.94, -26.91) * mm, "end": v(2.08, -26.63) * mm});
            skLineSegment(sketch, "E713", {"start": v(2.08, -26.63) * mm, "end": v(2.21, -26.35) * mm});
            skLineSegment(sketch, "E714", {"start": v(2.21, -26.35) * mm, "end": v(2.33, -26.08) * mm});
            skLineSegment(sketch, "E715", {"start": v(2.33, -26.08) * mm, "end": v(2.43, -25.82) * mm});
            skLineSegment(sketch, "E716", {"start": v(2.43, -25.82) * mm, "end": v(2.53, -25.57) * mm});
            skLineSegment(sketch, "E717", {"start": v(2.53, -25.57) * mm, "end": v(2.62, -25.33) * mm});
            skLineSegment(sketch, "E718", {"start": v(2.62, -25.33) * mm, "end": v(2.7, -25.1) * mm});
            skLineSegment(sketch, "E719", {"start": v(2.7, -25.1) * mm, "end": v(2.76, -24.88) * mm});
            skLineSegment(sketch, "E720", {"start": v(2.76, -24.88) * mm, "end": v(2.82, -24.67) * mm});
            skLineSegment(sketch, "E721", {"start": v(2.82, -24.67) * mm, "end": v(2.87, -24.47) * mm});
            skLineSegment(sketch, "E722", {"start": v(2.87, -24.47) * mm, "end": v(2.91, -24.28) * mm});
            skLineSegment(sketch, "E723", {"start": v(2.91, -24.28) * mm, "end": v(2.95, -24.1) * mm});
            skLineSegment(sketch, "E724", {"start": v(2.95, -24.1) * mm, "end": v(2.98, -23.94) * mm});
            skLineSegment(sketch, "E725", {"start": v(2.98, -23.94) * mm, "end": v(3, -23.79) * mm});
            skLineSegment(sketch, "E726", {"start": v(3, -23.79) * mm, "end": v(3.02, -23.65) * mm});
            skLineSegment(sketch, "E727", {"start": v(3.02, -23.65) * mm, "end": v(3.03, -23.52) * mm});
            skLineSegment(sketch, "E728", {"start": v(3.03, -23.52) * mm, "end": v(3.04, -23.4) * mm});
            skLineSegment(sketch, "E729", {"start": v(3.04, -23.4) * mm, "end": v(3.05, -23.3) * mm});
            skLineSegment(sketch, "E730", {"start": v(3.05, -23.3) * mm, "end": v(3.05, -23.2) * mm});
            skLineSegment(sketch, "E731", {"start": v(3.05, -23.2) * mm, "end": v(3.06, -23.13) * mm});
            skLineSegment(sketch, "E732", {"start": v(3.06, -23.13) * mm, "end": v(3.05, -23.06) * mm});
            skLineSegment(sketch, "E733", {"start": v(3.05, -23.06) * mm, "end": v(3.05, -23) * mm});
            skLineSegment(sketch, "E734", {"start": v(3.05, -23) * mm, "end": v(3.05, -22.97) * mm});
            skLineSegment(sketch, "E735", {"start": v(3.05, -22.97) * mm, "end": v(3.05, -22.94) * mm});
            skLineSegment(sketch, "E736", {"start": v(3.05, -22.94) * mm, "end": v(3.05, -22.92) * mm});
            skLineSegment(sketch, "E737", {"start": v(3.05, -22.92) * mm, "end": v(2.75, -20.63) * mm});
            skLineSegment(sketch, "E738", {"start": v(2.75, -20.63) * mm, "end": v(6.52, -19.78) * mm});
            skLineSegment(sketch, "E739", {"start": v(6.52, -19.78) * mm, "end": v(7.23, -21.98) * mm});
            skLineSegment(sketch, "E740", {"start": v(7.23, -21.98) * mm, "end": v(7.24, -22) * mm});
            skLineSegment(sketch, "E741", {"start": v(7.24, -22) * mm, "end": v(7.25, -22.02) * mm});
            skLineSegment(sketch, "E742", {"start": v(7.25, -22.02) * mm, "end": v(7.26, -22.06) * mm});
            skLineSegment(sketch, "E743", {"start": v(7.26, -22.06) * mm, "end": v(7.28, -22.1) * mm});
            skLineSegment(sketch, "E744", {"start": v(7.28, -22.1) * mm, "end": v(7.31, -22.17) * mm});
            skLineSegment(sketch, "E745", {"start": v(7.31, -22.17) * mm, "end": v(7.35, -22.24) * mm});
            skLineSegment(sketch, "E746", {"start": v(7.35, -22.24) * mm, "end": v(7.39, -22.32) * mm});
            skLineSegment(sketch, "E747", {"start": v(7.39, -22.32) * mm, "end": v(7.44, -22.41) * mm});
            skLineSegment(sketch, "E748", {"start": v(7.44, -22.41) * mm, "end": v(7.5, -22.51) * mm});
            skLineSegment(sketch, "E749", {"start": v(7.5, -22.51) * mm, "end": v(7.57, -22.62) * mm});
            skLineSegment(sketch, "E750", {"start": v(7.57, -22.62) * mm, "end": v(7.64, -22.74) * mm});
            skLineSegment(sketch, "E751", {"start": v(7.64, -22.74) * mm, "end": v(7.73, -22.87) * mm});
            skLineSegment(sketch, "E752", {"start": v(7.73, -22.87) * mm, "end": v(7.83, -23) * mm});
            skLineSegment(sketch, "E753", {"start": v(7.83, -23) * mm, "end": v(7.94, -23.15) * mm});
            skLineSegment(sketch, "E754", {"start": v(7.94, -23.15) * mm, "end": v(8.06, -23.3) * mm});
            skLineSegment(sketch, "E755", {"start": v(8.06, -23.3) * mm, "end": v(8.19, -23.46) * mm});
            skLineSegment(sketch, "E756", {"start": v(8.19, -23.46) * mm, "end": v(8.33, -23.62) * mm});
            skLineSegment(sketch, "E757", {"start": v(8.33, -23.62) * mm, "end": v(8.48, -23.8) * mm});
            skLineSegment(sketch, "E758", {"start": v(8.48, -23.8) * mm, "end": v(8.65, -23.97) * mm});
            skLineSegment(sketch, "E759", {"start": v(8.65, -23.97) * mm, "end": v(8.83, -24.15) * mm});
            skLineSegment(sketch, "E760", {"start": v(8.83, -24.15) * mm, "end": v(9.03, -24.33) * mm});
            skLineSegment(sketch, "E761", {"start": v(9.03, -24.33) * mm, "end": v(9.23, -24.52) * mm});
            skLineSegment(sketch, "E762", {"start": v(9.23, -24.52) * mm, "end": v(9.46, -24.72) * mm});
            skLineSegment(sketch, "E763", {"start": v(9.46, -24.72) * mm, "end": v(9.7, -24.91) * mm});
            skLineSegment(sketch, "E764", {"start": v(9.7, -24.91) * mm, "end": v(9.94, -25.1) * mm});
            skLineSegment(sketch, "E765", {"start": v(9.94, -25.1) * mm, "end": v(10.2, -25.3) * mm});
            skLineSegment(sketch, "E766", {"start": v(10.2, -25.3) * mm, "end": v(10.49, -25.5) * mm});
            skLineSegment(sketch, "E767", {"start": v(10.49, -25.5) * mm, "end": v(10.78, -25.7) * mm});
            skLineSegment(sketch, "E768", {"start": v(10.78, -25.7) * mm, "end": v(11, -25.7) * mm});
            skLineSegment(sketch, "E769", {"start": v(11, -25.7) * mm, "end": v(12.56, -24.97) * mm});
            skLineSegment(sketch, "E770", {"start": v(12.56, -24.97) * mm, "end": v(12.71, -24.82) * mm});
            skLineSegment(sketch, "E771", {"start": v(12.71, -24.82) * mm, "end": v(12.75, -24.47) * mm});
            skLineSegment(sketch, "E772", {"start": v(12.75, -24.47) * mm, "end": v(12.78, -24.12) * mm});
            skLineSegment(sketch, "E773", {"start": v(12.78, -24.12) * mm, "end": v(12.8, -23.8) * mm});
            skLineSegment(sketch, "E774", {"start": v(12.8, -23.8) * mm, "end": v(12.81, -23.47) * mm});
            skLineSegment(sketch, "E775", {"start": v(12.81, -23.47) * mm, "end": v(12.82, -23.17) * mm});
            skLineSegment(sketch, "E776", {"start": v(12.82, -23.17) * mm, "end": v(12.82, -22.87) * mm});
            skLineSegment(sketch, "E777", {"start": v(12.82, -22.87) * mm, "end": v(12.8, -22.6) * mm});
            skLineSegment(sketch, "E778", {"start": v(12.8, -22.6) * mm, "end": v(12.8, -22.33) * mm});
            skLineSegment(sketch, "E779", {"start": v(12.8, -22.33) * mm, "end": v(12.77, -22.07) * mm});
            skLineSegment(sketch, "E780", {"start": v(12.77, -22.07) * mm, "end": v(12.75, -21.83) * mm});
            skLineSegment(sketch, "E781", {"start": v(12.75, -21.83) * mm, "end": v(12.72, -21.6) * mm});
            skLineSegment(sketch, "E782", {"start": v(12.72, -21.6) * mm, "end": v(12.69, -21.38) * mm});
            skLineSegment(sketch, "E783", {"start": v(12.69, -21.38) * mm, "end": v(12.65, -21.18) * mm});
            skLineSegment(sketch, "E784", {"start": v(12.65, -21.18) * mm, "end": v(12.62, -21) * mm});
            skLineSegment(sketch, "E785", {"start": v(12.62, -21) * mm, "end": v(12.58, -20.82) * mm});
            skLineSegment(sketch, "E786", {"start": v(12.58, -20.82) * mm, "end": v(12.54, -20.66) * mm});
            skLineSegment(sketch, "E787", {"start": v(12.54, -20.66) * mm, "end": v(12.5, -20.5) * mm});
            skLineSegment(sketch, "E788", {"start": v(12.5, -20.5) * mm, "end": v(12.46, -20.37) * mm});
            skLineSegment(sketch, "E789", {"start": v(12.46, -20.37) * mm, "end": v(12.42, -20.25) * mm});
            skLineSegment(sketch, "E790", {"start": v(12.42, -20.25) * mm, "end": v(12.38, -20.14) * mm});
            skLineSegment(sketch, "E791", {"start": v(12.38, -20.14) * mm, "end": v(12.34, -20.04) * mm});
            skLineSegment(sketch, "E792", {"start": v(12.34, -20.04) * mm, "end": v(12.3, -19.95) * mm});
            skLineSegment(sketch, "E793", {"start": v(12.3, -19.95) * mm, "end": v(12.28, -19.88) * mm});
            skLineSegment(sketch, "E794", {"start": v(12.28, -19.88) * mm, "end": v(12.25, -19.82) * mm});
            skLineSegment(sketch, "E795", {"start": v(12.25, -19.82) * mm, "end": v(12.23, -19.77) * mm});
            skLineSegment(sketch, "E796", {"start": v(12.23, -19.77) * mm, "end": v(12.2, -19.74) * mm});
            skLineSegment(sketch, "E797", {"start": v(12.2, -19.74) * mm, "end": v(12.2, -19.71) * mm});
            skLineSegment(sketch, "E798", {"start": v(12.2, -19.71) * mm, "end": v(12.19, -19.7) * mm});
            skLineSegment(sketch, "E799", {"start": v(12.19, -19.7) * mm, "end": v(10.98, -17.73) * mm});
            skLineSegment(sketch, "E800", {"start": v(10.98, -17.73) * mm, "end": v(14.08, -15.42) * mm});
            skLineSegment(sketch, "E801", {"start": v(14.08, -15.42) * mm, "end": v(15.63, -17.13) * mm});
            skLineSegment(sketch, "E802", {"start": v(15.63, -17.13) * mm, "end": v(15.64, -17.14) * mm});
            skLineSegment(sketch, "E803", {"start": v(15.64, -17.14) * mm, "end": v(15.66, -17.16) * mm});
            skLineSegment(sketch, "E804", {"start": v(15.66, -17.16) * mm, "end": v(15.69, -17.2) * mm});
            skLineSegment(sketch, "E805", {"start": v(15.69, -17.2) * mm, "end": v(15.73, -17.23) * mm});
            skLineSegment(sketch, "E806", {"start": v(15.73, -17.23) * mm, "end": v(15.78, -17.27) * mm});
            skLineSegment(sketch, "E807", {"start": v(15.78, -17.27) * mm, "end": v(15.84, -17.32) * mm});
            skLineSegment(sketch, "E808", {"start": v(15.84, -17.32) * mm, "end": v(15.9, -17.38) * mm});
            skLineSegment(sketch, "E809", {"start": v(15.9, -17.38) * mm, "end": v(16, -17.44) * mm});
            skLineSegment(sketch, "E810", {"start": v(16, -17.44) * mm, "end": v(16.09, -17.5) * mm});
            skLineSegment(sketch, "E811", {"start": v(16.09, -17.5) * mm, "end": v(16.2, -17.58) * mm});
            skLineSegment(sketch, "E812", {"start": v(16.2, -17.58) * mm, "end": v(16.31, -17.66) * mm});
            skLineSegment(sketch, "E813", {"start": v(16.31, -17.66) * mm, "end": v(16.44, -17.74) * mm});
            skLineSegment(sketch, "E814", {"start": v(16.44, -17.74) * mm, "end": v(16.59, -17.83) * mm});
            skLineSegment(sketch, "E815", {"start": v(16.59, -17.83) * mm, "end": v(16.75, -17.91) * mm});
            skLineSegment(sketch, "E816", {"start": v(16.75, -17.91) * mm, "end": v(16.92, -18) * mm});
            skLineSegment(sketch, "E817", {"start": v(16.92, -18) * mm, "end": v(17.1, -18.1) * mm});
            skLineSegment(sketch, "E818", {"start": v(17.1, -18.1) * mm, "end": v(17.3, -18.19) * mm});
            skLineSegment(sketch, "E819", {"start": v(17.3, -18.19) * mm, "end": v(17.5, -18.28) * mm});
            skLineSegment(sketch, "E820", {"start": v(17.5, -18.28) * mm, "end": v(17.73, -18.37) * mm});
            skLineSegment(sketch, "E821", {"start": v(17.73, -18.37) * mm, "end": v(17.97, -18.46) * mm});
            skLineSegment(sketch, "E822", {"start": v(17.97, -18.46) * mm, "end": v(18.22, -18.55) * mm});
            skLineSegment(sketch, "E823", {"start": v(18.22, -18.55) * mm, "end": v(18.5, -18.64) * mm});
            skLineSegment(sketch, "E824", {"start": v(18.5, -18.64) * mm, "end": v(18.77, -18.73) * mm});
            skLineSegment(sketch, "E825", {"start": v(18.77, -18.73) * mm, "end": v(19.07, -18.8) * mm});
            skLineSegment(sketch, "E826", {"start": v(19.07, -18.8) * mm, "end": v(19.38, -18.89) * mm});
            skLineSegment(sketch, "E827", {"start": v(19.38, -18.89) * mm, "end": v(19.7, -18.96) * mm});
            skLineSegment(sketch, "E828", {"start": v(19.7, -18.96) * mm, "end": v(20.04, -19.03) * mm});
            skLineSegment(sketch, "E829", {"start": v(20.04, -19.03) * mm, "end": v(20.39, -19.1) * mm});
            skLineSegment(sketch, "E830", {"start": v(20.39, -19.1) * mm, "end": v(20.58, -19) * mm});
            skLineSegment(sketch, "E831", {"start": v(20.58, -19) * mm, "end": v(21.7, -17.7) * mm});
            skLineSegment(sketch, "E832", {"start": v(21.7, -17.7) * mm, "end": v(21.79, -17.5) * mm});
            skLineSegment(sketch, "E833", {"start": v(21.79, -17.5) * mm, "end": v(21.68, -17.16) * mm});
            skLineSegment(sketch, "E834", {"start": v(21.68, -17.16) * mm, "end": v(21.57, -16.83) * mm});
            skLineSegment(sketch, "E835", {"start": v(21.57, -16.83) * mm, "end": v(21.45, -16.52) * mm});
            skLineSegment(sketch, "E836", {"start": v(21.45, -16.52) * mm, "end": v(21.33, -16.23) * mm});
            skLineSegment(sketch, "E837", {"start": v(21.33, -16.23) * mm, "end": v(21.21, -15.95) * mm});
            skLineSegment(sketch, "E838", {"start": v(21.21, -15.95) * mm, "end": v(21.1, -15.68) * mm});
            skLineSegment(sketch, "E839", {"start": v(21.1, -15.68) * mm, "end": v(20.97, -15.42) * mm});
            skLineSegment(sketch, "E840", {"start": v(20.97, -15.42) * mm, "end": v(20.85, -15.19) * mm});
            skLineSegment(sketch, "E841", {"start": v(20.85, -15.19) * mm, "end": v(20.73, -14.96) * mm});
            skLineSegment(sketch, "E842", {"start": v(20.73, -14.96) * mm, "end": v(20.6, -14.75) * mm});
            skLineSegment(sketch, "E843", {"start": v(20.6, -14.75) * mm, "end": v(20.49, -14.55) * mm});
            skLineSegment(sketch, "E844", {"start": v(20.49, -14.55) * mm, "end": v(20.37, -14.37) * mm});
            skLineSegment(sketch, "E845", {"start": v(20.37, -14.37) * mm, "end": v(20.25, -14.2) * mm});
            skLineSegment(sketch, "E846", {"start": v(20.25, -14.2) * mm, "end": v(20.14, -14.04) * mm});
            skLineSegment(sketch, "E847", {"start": v(20.14, -14.04) * mm, "end": v(20.04, -13.9) * mm});
            skLineSegment(sketch, "E848", {"start": v(20.04, -13.9) * mm, "end": v(19.93, -13.76) * mm});
            skLineSegment(sketch, "E849", {"start": v(19.93, -13.76) * mm, "end": v(19.84, -13.64) * mm});
            skLineSegment(sketch, "E850", {"start": v(19.84, -13.64) * mm, "end": v(19.75, -13.54) * mm});
            skLineSegment(sketch, "E851", {"start": v(19.75, -13.54) * mm, "end": v(19.66, -13.44) * mm});
            skLineSegment(sketch, "E852", {"start": v(19.66, -13.44) * mm, "end": v(19.58, -13.35) * mm});
            skLineSegment(sketch, "E853", {"start": v(19.58, -13.35) * mm, "end": v(19.5, -13.28) * mm});
            skLineSegment(sketch, "E854", {"start": v(19.5, -13.28) * mm, "end": v(19.44, -13.22) * mm});
            skLineSegment(sketch, "E855", {"start": v(19.44, -13.22) * mm, "end": v(19.38, -13.16) * mm});
            skLineSegment(sketch, "E856", {"start": v(19.38, -13.16) * mm, "end": v(19.33, -13.12) * mm});
            skLineSegment(sketch, "E857", {"start": v(19.33, -13.12) * mm, "end": v(19.3, -13.08) * mm});
            skLineSegment(sketch, "E858", {"start": v(19.3, -13.08) * mm, "end": v(19.26, -13.06) * mm});
            skLineSegment(sketch, "E859", {"start": v(19.26, -13.06) * mm, "end": v(19.24, -13.04) * mm});
            skLineSegment(sketch, "E860", {"start": v(19.24, -13.04) * mm, "end": v(19.22, -13.03) * mm});
            skLineSegment(sketch, "E861", {"start": v(19.22, -13.03) * mm, "end": v(17.32, -11.72) * mm});
            skLineSegment(sketch, "E862", {"start": v(17.32, -11.72) * mm, "end": v(19.21, -8.35) * mm});
            skLineSegment(sketch, "E863", {"start": v(19.21, -8.35) * mm, "end": v(21.32, -9.3) * mm});
            skLineSegment(sketch, "E864", {"start": v(21.32, -9.3) * mm, "end": v(21.34, -9.3) * mm});
            skLineSegment(sketch, "E865", {"start": v(21.34, -9.3) * mm, "end": v(21.36, -9.3) * mm});
            skLineSegment(sketch, "E866", {"start": v(21.36, -9.3) * mm, "end": v(21.4, -9.32) * mm});
            skLineSegment(sketch, "E867", {"start": v(21.4, -9.32) * mm, "end": v(21.45, -9.34) * mm});
            skLineSegment(sketch, "E868", {"start": v(21.45, -9.34) * mm, "end": v(21.52, -9.36) * mm});
            skLineSegment(sketch, "E869", {"start": v(21.52, -9.36) * mm, "end": v(21.6, -9.38) * mm});
            skLineSegment(sketch, "E870", {"start": v(21.6, -9.38) * mm, "end": v(21.68, -9.4) * mm});
            skLineSegment(sketch, "E871", {"start": v(21.68, -9.4) * mm, "end": v(21.78, -9.42) * mm});
            skLineSegment(sketch, "E872", {"start": v(21.78, -9.42) * mm, "end": v(21.9, -9.45) * mm});
            skLineSegment(sketch, "E873", {"start": v(21.9, -9.45) * mm, "end": v(22.03, -9.47) * mm});
            skLineSegment(sketch, "E874", {"start": v(22.03, -9.47) * mm, "end": v(22.17, -9.5) * mm});
            skLineSegment(sketch, "E875", {"start": v(22.17, -9.5) * mm, "end": v(22.32, -9.51) * mm});
            skLineSegment(sketch, "E876", {"start": v(22.32, -9.51) * mm, "end": v(22.48, -9.53) * mm});
            skLineSegment(sketch, "E877", {"start": v(22.48, -9.53) * mm, "end": v(22.66, -9.55) * mm});
            skLineSegment(sketch, "E878", {"start": v(22.66, -9.55) * mm, "end": v(22.86, -9.56) * mm});
            skLineSegment(sketch, "E879", {"start": v(22.86, -9.56) * mm, "end": v(23.06, -9.57) * mm});
            skLineSegment(sketch, "E880", {"start": v(23.06, -9.57) * mm, "end": v(23.28, -9.57) * mm});
            skLineSegment(sketch, "E881", {"start": v(23.28, -9.57) * mm, "end": v(23.5, -9.57) * mm});
            skLineSegment(sketch, "E882", {"start": v(23.5, -9.57) * mm, "end": v(23.75, -9.56) * mm});
            skLineSegment(sketch, "E883", {"start": v(23.75, -9.56) * mm, "end": v(24, -9.55) * mm});
            skLineSegment(sketch, "E884", {"start": v(24, -9.55) * mm, "end": v(24.27, -9.53) * mm});
            skLineSegment(sketch, "E885", {"start": v(24.27, -9.53) * mm, "end": v(24.55, -9.5) * mm});
            skLineSegment(sketch, "E886", {"start": v(24.55, -9.5) * mm, "end": v(24.84, -9.47) * mm});
            skLineSegment(sketch, "E887", {"start": v(24.84, -9.47) * mm, "end": v(25.15, -9.42) * mm});
            skLineSegment(sketch, "E888", {"start": v(25.15, -9.42) * mm, "end": v(25.46, -9.37) * mm});
            skLineSegment(sketch, "E889", {"start": v(25.46, -9.37) * mm, "end": v(25.79, -9.3) * mm});
            skLineSegment(sketch, "E890", {"start": v(25.79, -9.3) * mm, "end": v(26.12, -9.23) * mm});
            skLineSegment(sketch, "E891", {"start": v(26.12, -9.23) * mm, "end": v(26.47, -9.15) * mm});
            skLineSegment(sketch, "E892", {"start": v(26.47, -9.15) * mm, "end": v(26.6, -8.97) * mm});
            skLineSegment(sketch, "E893", {"start": v(26.6, -8.97) * mm, "end": v(27.11, -7.33) * mm});
            skLineSegment(sketch, "E894", {"start": v(27.11, -7.33) * mm, "end": v(27.1, -7.12) * mm});
            skLineSegment(sketch, "E895", {"start": v(27.1, -7.12) * mm, "end": v(26.86, -6.85) * mm});
            skLineSegment(sketch, "E896", {"start": v(26.86, -6.85) * mm, "end": v(26.63, -6.6) * mm});
            skLineSegment(sketch, "E897", {"start": v(26.63, -6.6) * mm, "end": v(26.4, -6.36) * mm});
            skLineSegment(sketch, "E898", {"start": v(26.4, -6.36) * mm, "end": v(26.17, -6.14) * mm});
            skLineSegment(sketch, "E899", {"start": v(26.17, -6.14) * mm, "end": v(25.94, -5.93) * mm});
            skLineSegment(sketch, "E900", {"start": v(25.94, -5.93) * mm, "end": v(25.73, -5.74) * mm});
            skLineSegment(sketch, "E901", {"start": v(25.73, -5.74) * mm, "end": v(25.51, -5.56) * mm});
            skLineSegment(sketch, "E902", {"start": v(25.51, -5.56) * mm, "end": v(25.3, -5.39) * mm});
            skLineSegment(sketch, "E903", {"start": v(25.3, -5.39) * mm, "end": v(25.1, -5.23) * mm});
            skLineSegment(sketch, "E904", {"start": v(25.1, -5.23) * mm, "end": v(24.9, -5.09) * mm});
            skLineSegment(sketch, "E905", {"start": v(24.9, -5.09) * mm, "end": v(24.71, -4.96) * mm});
            skLineSegment(sketch, "E906", {"start": v(24.71, -4.96) * mm, "end": v(24.53, -4.84) * mm});
            skLineSegment(sketch, "E907", {"start": v(24.53, -4.84) * mm, "end": v(24.36, -4.73) * mm});
            skLineSegment(sketch, "E908", {"start": v(24.36, -4.73) * mm, "end": v(24.2, -4.63) * mm});
            skLineSegment(sketch, "E909", {"start": v(24.2, -4.63) * mm, "end": v(24.04, -4.54) * mm});
            skLineSegment(sketch, "E910", {"start": v(24.04, -4.54) * mm, "end": v(23.89, -4.46) * mm});
            skLineSegment(sketch, "E911", {"start": v(23.89, -4.46) * mm, "end": v(23.75, -4.4) * mm});
            skLineSegment(sketch, "E912", {"start": v(23.75, -4.4) * mm, "end": v(23.62, -4.33) * mm});
            skLineSegment(sketch, "E913", {"start": v(23.62, -4.33) * mm, "end": v(23.5, -4.28) * mm});
            skLineSegment(sketch, "E914", {"start": v(23.5, -4.28) * mm, "end": v(23.4, -4.23) * mm});
            skLineSegment(sketch, "E915", {"start": v(23.4, -4.23) * mm, "end": v(23.3, -4.2) * mm});
            skLineSegment(sketch, "E916", {"start": v(23.3, -4.2) * mm, "end": v(23.22, -4.16) * mm});
            skLineSegment(sketch, "E917", {"start": v(23.22, -4.16) * mm, "end": v(23.14, -4.14) * mm});
            skLineSegment(sketch, "E918", {"start": v(23.14, -4.14) * mm, "end": v(23.08, -4.11) * mm});
            skLineSegment(sketch, "E919", {"start": v(23.08, -4.11) * mm, "end": v(23.03, -4.1) * mm});
            skLineSegment(sketch, "E920", {"start": v(23.03, -4.1) * mm, "end": v(22.99, -4.09) * mm});
            skLineSegment(sketch, "E921", {"start": v(22.99, -4.09) * mm, "end": v(22.96, -4.08) * mm});
            skLineSegment(sketch, "E922", {"start": v(22.96, -4.08) * mm, "end": v(22.94, -4.08) * mm});
            skLineSegment(sketch, "E923", {"start": v(22.94, -4.08) * mm, "end": v(20.67, -3.66) * mm});
            skLineSegment(sketch, "E924", {"start": v(20.67, -3.66) * mm, "end": v(21.03, 0.2) * mm});
            skLineSegment(sketch, "E925", {"start": v(-11.75, 20.55) * mm, "end": v(-11.8, 20.6) * mm});
            skCircle(sketch, "E926", {"center": v(0.03, 0.2) * mm, "radius": 1.59 * mm});
            skSolve(sketch);
        }
        {
            var Q0;
            Q0=makeQuery(id+"F0.imprint","IMPRINT",FACE,{"disambiguationData":[TD([[makeQuery(id+"F0.imprint","IMPRINT",EDGE,{"derivedFrom":sQuery(id+"F0.wireOp",EDGE,"E0")}),1.0]])]});
            extrude(context, id + "F1", {"entities" : qUnion([Q0]), "depth" : 2.97 * mm});
        }
    });
